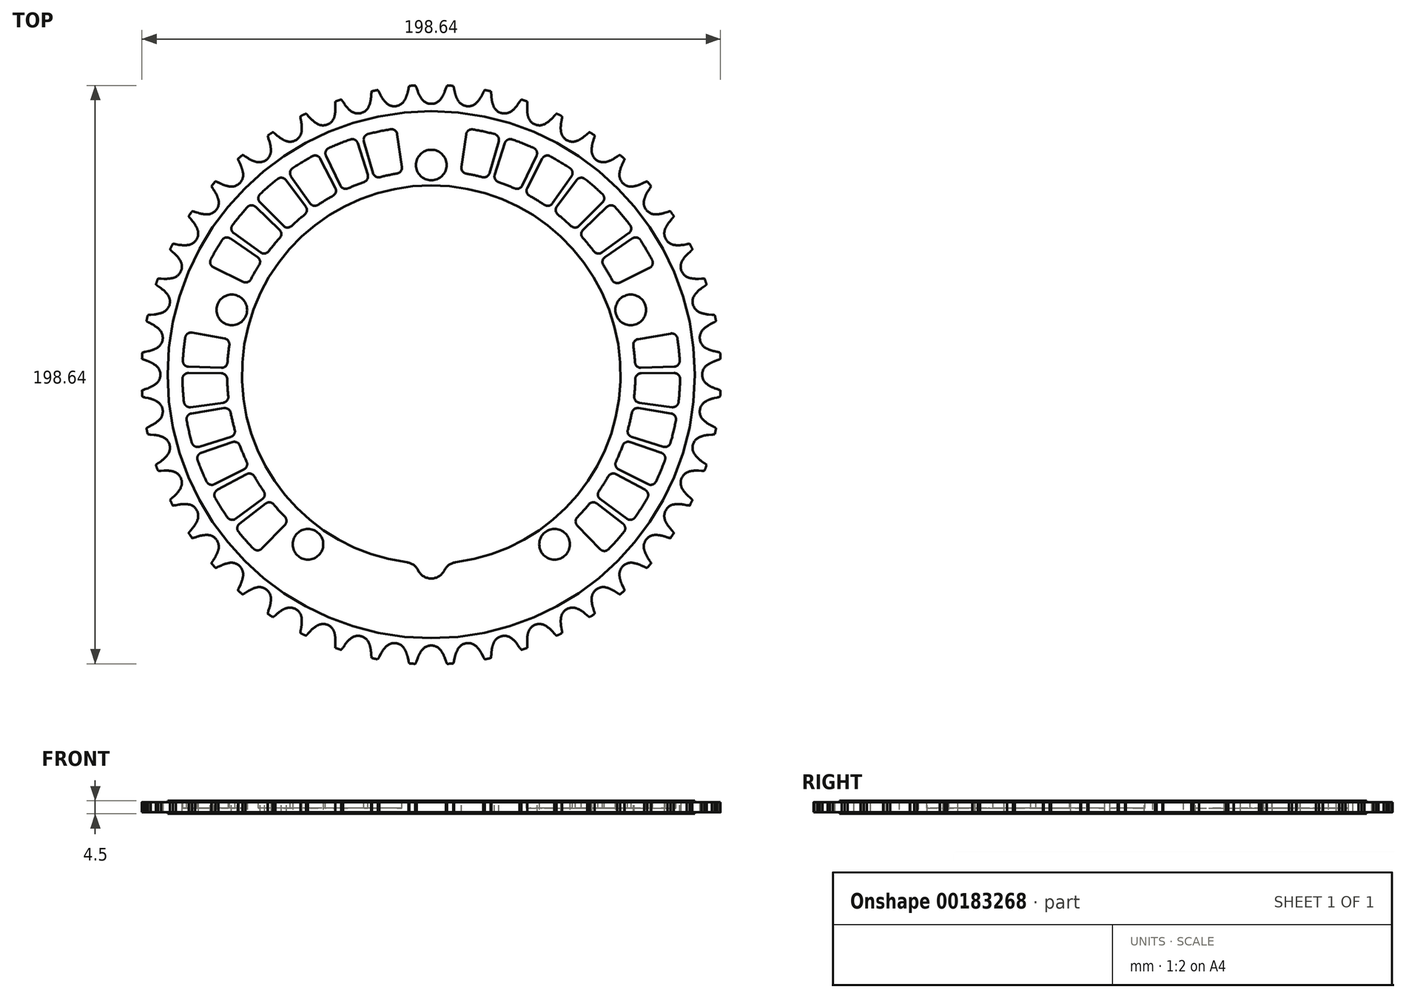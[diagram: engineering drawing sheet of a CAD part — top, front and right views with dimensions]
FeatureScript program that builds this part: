
annotation { "Feature Type Name" : "Feature", "Feature Type Description" : "" }
export const myFeature = defineFeature(function(context is Context, id is Id, definition is map)
    precondition{}
    {
        {
            var Q0;
            Q0=qCreatedBy(makeId("Top.planeOp"),FACE);
            var sketch = newSketch(context, id + "F0", { "sketchPlane" : qUnion([Q0])});
            skCircle(sketch, "E0", {"center": v(0, 0) * mm, "radius": 97.02 * mm, "construction": true});
            skArc(sketch, "E1", {"start": v(-4.67, 97.33) * mm, "mid": v(-4.05, 95.93) * mm, "end": v(-3.24, 94.65) * mm});
            skLineSegment(sketch, "E2", {"start": v(-4.67, 97.33) * mm, "end": v(-5.03, 98.35) * mm});
            skArc(sketch, "E3.trimOffspring", {"start": v(-3.24, 94.65) * mm, "mid": v(-1.81, 93.44) * mm, "end": v(0, 93) * mm});
            skArc(sketch, "E4.trimOffspring", {"start": v(-5.03, 98.35) * mm, "mid": v(-5.68, 99.7) * mm, "end": v(-6.61, 100.86) * mm});
            skArc(sketch, "E5.MirrorCS", {"start": v(3.24, 94.65) * mm, "mid": v(1.81, 93.44) * mm, "end": v(0, 93) * mm});
            skArc(sketch, "E6.MirrorCS", {"start": v(4.67, 97.33) * mm, "mid": v(4.05, 95.93) * mm, "end": v(3.24, 94.65) * mm});
            skLineSegment(sketch, "E7.MirrorCS", {"start": v(4.67, 97.33) * mm, "end": v(5.03, 98.35) * mm});
            skArc(sketch, "E8.MirrorCS", {"start": v(5.03, 98.35) * mm, "mid": v(5.68, 99.7) * mm, "end": v(6.61, 100.86) * mm});
            skCircle(sketch, "E9", {"center": v(0, 0) * mm, "radius": 99.47 * mm});
            skArc(sketch, "E10.1.0", {"start": v(-17.83, 96.85) * mm, "mid": v(-18.64, 98.1) * mm, "end": v(-19.72, 99.14) * mm});
            skLineSegment(sketch, "E10.1.1", {"start": v(-17.34, 95.88) * mm, "end": v(-17.83, 96.85) * mm});
            skArc(sketch, "E10.1.2", {"start": v(-17.34, 95.88) * mm, "mid": v(-16.54, 94.58) * mm, "end": v(-15.56, 93.41) * mm});
            skArc(sketch, "E10.1.3", {"start": v(-15.56, 93.41) * mm, "mid": v(-14, 92.4) * mm, "end": v(-12.14, 92.2) * mm});
            skArc(sketch, "E10.1.4", {"start": v(-9.14, 94.26) * mm, "mid": v(-10.4, 92.88) * mm, "end": v(-12.14, 92.2) * mm});
            skArc(sketch, "E10.1.5", {"start": v(-8.07, 97.1) * mm, "mid": v(-8.5, 95.64) * mm, "end": v(-9.14, 94.26) * mm});
            skLineSegment(sketch, "E10.1.6", {"start": v(-8.07, 97.1) * mm, "end": v(-7.85, 98.17) * mm});
            skArc(sketch, "E10.1.7", {"start": v(-7.85, 98.17) * mm, "mid": v(-7.39, 99.59) * mm, "end": v(-6.61, 100.86) * mm});
            skArc(sketch, "E10.2.0", {"start": v(-30.32, 93.7) * mm, "mid": v(-31.29, 94.83) * mm, "end": v(-32.5, 95.72) * mm});
            skLineSegment(sketch, "E10.2.1", {"start": v(-29.7, 92.8) * mm, "end": v(-30.32, 93.7) * mm});
            skArc(sketch, "E10.2.2", {"start": v(-29.7, 92.8) * mm, "mid": v(-28.74, 91.61) * mm, "end": v(-27.62, 90.58) * mm});
            skArc(sketch, "E10.2.3", {"start": v(-27.62, 90.58) * mm, "mid": v(-25.94, 89.79) * mm, "end": v(-24.07, 89.84) * mm});
            skArc(sketch, "E10.2.4", {"start": v(-21.37, 92.26) * mm, "mid": v(-22.43, 90.72) * mm, "end": v(-24.07, 89.84) * mm});
            skArc(sketch, "E10.2.5", {"start": v(-20.68, 95.22) * mm, "mid": v(-20.91, 93.71) * mm, "end": v(-21.37, 92.26) * mm});
            skLineSegment(sketch, "E10.2.6", {"start": v(-20.68, 95.22) * mm, "end": v(-20.6, 96.3) * mm});
            skArc(sketch, "E10.2.7", {"start": v(-20.6, 96.3) * mm, "mid": v(-20.32, 97.77) * mm, "end": v(-19.72, 99.14) * mm});
            skArc(sketch, "E10.3.0", {"start": v(-42.29, 88.94) * mm, "mid": v(-43.4, 89.94) * mm, "end": v(-44.7, 90.66) * mm});
            skLineSegment(sketch, "E10.3.1", {"start": v(-41.56, 88.13) * mm, "end": v(-42.29, 88.94) * mm});
            skArc(sketch, "E10.3.2", {"start": v(-41.56, 88.13) * mm, "mid": v(-40.46, 87.08) * mm, "end": v(-39.21, 86.2) * mm});
            skArc(sketch, "E10.3.3", {"start": v(-39.21, 86.2) * mm, "mid": v(-37.43, 85.63) * mm, "end": v(-35.6, 85.93) * mm});
            skArc(sketch, "E10.3.4", {"start": v(-33.23, 88.68) * mm, "mid": v(-34.08, 87.02) * mm, "end": v(-35.6, 85.93) * mm});
            skArc(sketch, "E10.3.5", {"start": v(-32.93, 91.7) * mm, "mid": v(-32.97, 90.18) * mm, "end": v(-33.23, 88.68) * mm});
            skLineSegment(sketch, "E10.3.6", {"start": v(-32.93, 91.7) * mm, "end": v(-32.99, 92.79) * mm});
            skArc(sketch, "E10.3.7", {"start": v(-32.99, 92.79) * mm, "mid": v(-32.91, 94.28) * mm, "end": v(-32.5, 95.72) * mm});
            skArc(sketch, "E10.4.0", {"start": v(-53.53, 82.66) * mm, "mid": v(-54.76, 83.5) * mm, "end": v(-56.16, 84.05) * mm});
            skLineSegment(sketch, "E10.4.1", {"start": v(-52.7, 81.95) * mm, "end": v(-53.53, 82.66) * mm});
            skArc(sketch, "E10.4.2", {"start": v(-52.7, 81.95) * mm, "mid": v(-51.48, 81.05) * mm, "end": v(-50.13, 80.35) * mm});
            skArc(sketch, "E10.4.3", {"start": v(-50.13, 80.35) * mm, "mid": v(-48.3, 80.01) * mm, "end": v(-46.5, 80.55) * mm});
            skArc(sketch, "E10.4.4", {"start": v(-44.52, 83.58) * mm, "mid": v(-45.15, 81.83) * mm, "end": v(-46.5, 80.55) * mm});
            skArc(sketch, "E10.4.5", {"start": v(-44.62, 86.62) * mm, "mid": v(-44.46, 85.1) * mm, "end": v(-44.52, 83.58) * mm});
            skLineSegment(sketch, "E10.4.6", {"start": v(-44.62, 86.62) * mm, "end": v(-44.82, 87.7) * mm});
            skArc(sketch, "E10.4.7", {"start": v(-44.82, 87.7) * mm, "mid": v(-44.93, 89.18) * mm, "end": v(-44.7, 90.66) * mm});
            skArc(sketch, "E10.5.0", {"start": v(-63.87, 74.96) * mm, "mid": v(-65.2, 75.64) * mm, "end": v(-66.65, 76) * mm});
            skLineSegment(sketch, "E10.5.1", {"start": v(-62.96, 74.37) * mm, "end": v(-63.87, 74.96) * mm});
            skArc(sketch, "E10.5.2", {"start": v(-62.96, 74.37) * mm, "mid": v(-61.62, 73.64) * mm, "end": v(-60.18, 73.12) * mm});
            skArc(sketch, "E10.5.3", {"start": v(-60.18, 73.12) * mm, "mid": v(-58.32, 73.03) * mm, "end": v(-56.62, 73.79) * mm});
            skArc(sketch, "E10.5.4", {"start": v(-55.05, 77.06) * mm, "mid": v(-55.44, 75.23) * mm, "end": v(-56.62, 73.79) * mm});
            skArc(sketch, "E10.5.5", {"start": v(-55.54, 80.06) * mm, "mid": v(-55.18, 78.58) * mm, "end": v(-55.05, 77.06) * mm});
            skLineSegment(sketch, "E10.5.6", {"start": v(-55.54, 80.06) * mm, "end": v(-55.88, 81.1) * mm});
            skArc(sketch, "E10.5.7", {"start": v(-55.88, 81.1) * mm, "mid": v(-56.2, 82.55) * mm, "end": v(-56.16, 84.05) * mm});
            skArc(sketch, "E10.6.0", {"start": v(-73.1, 65.98) * mm, "mid": v(-74.51, 66.49) * mm, "end": v(-76, 66.65) * mm});
            skLineSegment(sketch, "E10.6.1", {"start": v(-72.12, 65.51) * mm, "end": v(-73.1, 65.98) * mm});
            skArc(sketch, "E10.6.2", {"start": v(-72.12, 65.51) * mm, "mid": v(-70.7, 64.97) * mm, "end": v(-69.21, 64.64) * mm});
            skArc(sketch, "E10.6.3", {"start": v(-69.21, 64.64) * mm, "mid": v(-67.35, 64.79) * mm, "end": v(-65.76, 65.76) * mm});
            skArc(sketch, "E10.6.4", {"start": v(-64.64, 69.21) * mm, "mid": v(-64.79, 67.35) * mm, "end": v(-65.76, 65.76) * mm});
            skArc(sketch, "E10.6.5", {"start": v(-65.51, 72.12) * mm, "mid": v(-64.97, 70.7) * mm, "end": v(-64.64, 69.21) * mm});
            skLineSegment(sketch, "E10.6.6", {"start": v(-65.51, 72.12) * mm, "end": v(-65.98, 73.1) * mm});
            skArc(sketch, "E10.6.7", {"start": v(-65.98, 73.1) * mm, "mid": v(-66.49, 74.51) * mm, "end": v(-66.65, 76) * mm});
            skArc(sketch, "E10.7.0", {"start": v(-81.1, 55.88) * mm, "mid": v(-82.55, 56.2) * mm, "end": v(-84.05, 56.16) * mm});
            skLineSegment(sketch, "E10.7.1", {"start": v(-80.06, 55.54) * mm, "end": v(-81.1, 55.88) * mm});
            skArc(sketch, "E10.7.2", {"start": v(-80.06, 55.54) * mm, "mid": v(-78.58, 55.18) * mm, "end": v(-77.06, 55.05) * mm});
            skArc(sketch, "E10.7.3", {"start": v(-77.06, 55.05) * mm, "mid": v(-75.23, 55.44) * mm, "end": v(-73.79, 56.62) * mm});
            skArc(sketch, "E10.7.4", {"start": v(-73.12, 60.18) * mm, "mid": v(-73.03, 58.32) * mm, "end": v(-73.79, 56.62) * mm});
            skArc(sketch, "E10.7.5", {"start": v(-74.37, 62.96) * mm, "mid": v(-73.64, 61.62) * mm, "end": v(-73.12, 60.18) * mm});
            skLineSegment(sketch, "E10.7.6", {"start": v(-74.37, 62.96) * mm, "end": v(-74.96, 63.87) * mm});
            skArc(sketch, "E10.7.7", {"start": v(-74.96, 63.87) * mm, "mid": v(-75.64, 65.2) * mm, "end": v(-76, 66.65) * mm});
            skArc(sketch, "E10.8.0", {"start": v(-87.7, 44.82) * mm, "mid": v(-89.18, 44.93) * mm, "end": v(-90.66, 44.7) * mm});
            skLineSegment(sketch, "E10.8.1", {"start": v(-86.62, 44.62) * mm, "end": v(-87.7, 44.82) * mm});
            skArc(sketch, "E10.8.2", {"start": v(-86.62, 44.62) * mm, "mid": v(-85.1, 44.46) * mm, "end": v(-83.58, 44.52) * mm});
            skArc(sketch, "E10.8.3", {"start": v(-83.58, 44.52) * mm, "mid": v(-81.83, 45.15) * mm, "end": v(-80.55, 46.5) * mm});
            skArc(sketch, "E10.8.4", {"start": v(-80.35, 50.13) * mm, "mid": v(-80.01, 48.3) * mm, "end": v(-80.55, 46.5) * mm});
            skArc(sketch, "E10.8.5", {"start": v(-81.95, 52.7) * mm, "mid": v(-81.05, 51.48) * mm, "end": v(-80.35, 50.13) * mm});
            skLineSegment(sketch, "E10.8.6", {"start": v(-81.95, 52.7) * mm, "end": v(-82.66, 53.53) * mm});
            skArc(sketch, "E10.8.7", {"start": v(-82.66, 53.53) * mm, "mid": v(-83.5, 54.76) * mm, "end": v(-84.05, 56.16) * mm});
            skArc(sketch, "E10.9.0", {"start": v(-92.79, 32.99) * mm, "mid": v(-94.28, 32.91) * mm, "end": v(-95.72, 32.5) * mm});
            skLineSegment(sketch, "E10.9.1", {"start": v(-91.7, 32.93) * mm, "end": v(-92.79, 32.99) * mm});
            skArc(sketch, "E10.9.2", {"start": v(-91.7, 32.93) * mm, "mid": v(-90.18, 32.97) * mm, "end": v(-88.68, 33.23) * mm});
            skArc(sketch, "E10.9.3", {"start": v(-88.68, 33.23) * mm, "mid": v(-87.02, 34.08) * mm, "end": v(-85.93, 35.6) * mm});
            skArc(sketch, "E10.9.4", {"start": v(-86.2, 39.21) * mm, "mid": v(-85.63, 37.43) * mm, "end": v(-85.93, 35.6) * mm});
            skArc(sketch, "E10.9.5", {"start": v(-88.13, 41.56) * mm, "mid": v(-87.08, 40.46) * mm, "end": v(-86.2, 39.21) * mm});
            skLineSegment(sketch, "E10.9.6", {"start": v(-88.13, 41.56) * mm, "end": v(-88.94, 42.29) * mm});
            skArc(sketch, "E10.9.7", {"start": v(-88.94, 42.29) * mm, "mid": v(-89.94, 43.4) * mm, "end": v(-90.66, 44.7) * mm});
            skArc(sketch, "E10.10.0", {"start": v(-96.3, 20.6) * mm, "mid": v(-97.77, 20.32) * mm, "end": v(-99.14, 19.72) * mm});
            skLineSegment(sketch, "E10.10.1", {"start": v(-95.22, 20.68) * mm, "end": v(-96.3, 20.6) * mm});
            skArc(sketch, "E10.10.2", {"start": v(-95.22, 20.68) * mm, "mid": v(-93.71, 20.91) * mm, "end": v(-92.26, 21.37) * mm});
            skArc(sketch, "E10.10.3", {"start": v(-92.26, 21.37) * mm, "mid": v(-90.72, 22.43) * mm, "end": v(-89.84, 24.07) * mm});
            skArc(sketch, "E10.10.4", {"start": v(-90.58, 27.62) * mm, "mid": v(-89.79, 25.94) * mm, "end": v(-89.84, 24.07) * mm});
            skArc(sketch, "E10.10.5", {"start": v(-92.8, 29.7) * mm, "mid": v(-91.61, 28.74) * mm, "end": v(-90.58, 27.62) * mm});
            skLineSegment(sketch, "E10.10.6", {"start": v(-92.8, 29.7) * mm, "end": v(-93.7, 30.32) * mm});
            skArc(sketch, "E10.10.7", {"start": v(-93.7, 30.32) * mm, "mid": v(-94.83, 31.29) * mm, "end": v(-95.72, 32.5) * mm});
            skArc(sketch, "E10.11.0", {"start": v(-98.17, 7.85) * mm, "mid": v(-99.59, 7.39) * mm, "end": v(-100.86, 6.61) * mm});
            skLineSegment(sketch, "E10.11.1", {"start": v(-97.1, 8.07) * mm, "end": v(-98.17, 7.85) * mm});
            skArc(sketch, "E10.11.2", {"start": v(-97.1, 8.07) * mm, "mid": v(-95.64, 8.5) * mm, "end": v(-94.26, 9.14) * mm});
            skArc(sketch, "E10.11.3", {"start": v(-94.26, 9.14) * mm, "mid": v(-92.88, 10.4) * mm, "end": v(-92.2, 12.14) * mm});
            skArc(sketch, "E10.11.4", {"start": v(-93.41, 15.56) * mm, "mid": v(-92.4, 14) * mm, "end": v(-92.2, 12.14) * mm});
            skArc(sketch, "E10.11.5", {"start": v(-95.88, 17.34) * mm, "mid": v(-94.58, 16.54) * mm, "end": v(-93.41, 15.56) * mm});
            skLineSegment(sketch, "E10.11.6", {"start": v(-95.88, 17.34) * mm, "end": v(-96.85, 17.83) * mm});
            skArc(sketch, "E10.11.7", {"start": v(-96.85, 17.83) * mm, "mid": v(-98.1, 18.64) * mm, "end": v(-99.14, 19.72) * mm});
            skArc(sketch, "E10.12.0", {"start": v(-98.35, -5.03) * mm, "mid": v(-99.7, -5.68) * mm, "end": v(-100.86, -6.61) * mm});
            skLineSegment(sketch, "E10.12.1", {"start": v(-97.33, -4.67) * mm, "end": v(-98.35, -5.03) * mm});
            skArc(sketch, "E10.12.2", {"start": v(-97.33, -4.67) * mm, "mid": v(-95.93, -4.05) * mm, "end": v(-94.65, -3.24) * mm});
            skArc(sketch, "E10.12.3", {"start": v(-94.65, -3.24) * mm, "mid": v(-93.44, -1.81) * mm, "end": v(-93, 0) * mm});
            skArc(sketch, "E10.12.4", {"start": v(-94.65, 3.24) * mm, "mid": v(-93.44, 1.81) * mm, "end": v(-93, 0) * mm});
            skArc(sketch, "E10.12.5", {"start": v(-97.33, 4.67) * mm, "mid": v(-95.93, 4.05) * mm, "end": v(-94.65, 3.24) * mm});
            skLineSegment(sketch, "E10.12.6", {"start": v(-97.33, 4.67) * mm, "end": v(-98.35, 5.03) * mm});
            skArc(sketch, "E10.12.7", {"start": v(-98.35, 5.03) * mm, "mid": v(-99.7, 5.68) * mm, "end": v(-100.86, 6.61) * mm});
            skArc(sketch, "E10.13.0", {"start": v(-96.85, -17.83) * mm, "mid": v(-98.1, -18.64) * mm, "end": v(-99.14, -19.72) * mm});
            skLineSegment(sketch, "E10.13.1", {"start": v(-95.88, -17.34) * mm, "end": v(-96.85, -17.83) * mm});
            skArc(sketch, "E10.13.2", {"start": v(-95.88, -17.34) * mm, "mid": v(-94.58, -16.54) * mm, "end": v(-93.41, -15.56) * mm});
            skArc(sketch, "E10.13.3", {"start": v(-93.41, -15.56) * mm, "mid": v(-92.4, -14) * mm, "end": v(-92.2, -12.14) * mm});
            skArc(sketch, "E10.13.4", {"start": v(-94.26, -9.14) * mm, "mid": v(-92.88, -10.4) * mm, "end": v(-92.2, -12.14) * mm});
            skArc(sketch, "E10.13.5", {"start": v(-97.1, -8.07) * mm, "mid": v(-95.64, -8.5) * mm, "end": v(-94.26, -9.14) * mm});
            skLineSegment(sketch, "E10.13.6", {"start": v(-97.1, -8.07) * mm, "end": v(-98.17, -7.85) * mm});
            skArc(sketch, "E10.13.7", {"start": v(-98.17, -7.85) * mm, "mid": v(-99.59, -7.39) * mm, "end": v(-100.86, -6.61) * mm});
            skArc(sketch, "E10.14.0", {"start": v(-93.7, -30.32) * mm, "mid": v(-94.83, -31.29) * mm, "end": v(-95.72, -32.5) * mm});
            skLineSegment(sketch, "E10.14.1", {"start": v(-92.8, -29.7) * mm, "end": v(-93.7, -30.32) * mm});
            skArc(sketch, "E10.14.2", {"start": v(-92.8, -29.7) * mm, "mid": v(-91.61, -28.74) * mm, "end": v(-90.58, -27.62) * mm});
            skArc(sketch, "E10.14.3", {"start": v(-90.58, -27.62) * mm, "mid": v(-89.79, -25.94) * mm, "end": v(-89.84, -24.07) * mm});
            skArc(sketch, "E10.14.4", {"start": v(-92.26, -21.37) * mm, "mid": v(-90.72, -22.43) * mm, "end": v(-89.84, -24.07) * mm});
            skArc(sketch, "E10.14.5", {"start": v(-95.22, -20.68) * mm, "mid": v(-93.71, -20.91) * mm, "end": v(-92.26, -21.37) * mm});
            skLineSegment(sketch, "E10.14.6", {"start": v(-95.22, -20.68) * mm, "end": v(-96.3, -20.6) * mm});
            skArc(sketch, "E10.14.7", {"start": v(-96.3, -20.6) * mm, "mid": v(-97.77, -20.32) * mm, "end": v(-99.14, -19.72) * mm});
            skArc(sketch, "E10.15.0", {"start": v(-88.94, -42.29) * mm, "mid": v(-89.94, -43.4) * mm, "end": v(-90.66, -44.7) * mm});
            skLineSegment(sketch, "E10.15.1", {"start": v(-88.13, -41.56) * mm, "end": v(-88.94, -42.29) * mm});
            skArc(sketch, "E10.15.2", {"start": v(-88.13, -41.56) * mm, "mid": v(-87.08, -40.46) * mm, "end": v(-86.2, -39.21) * mm});
            skArc(sketch, "E10.15.3", {"start": v(-86.2, -39.21) * mm, "mid": v(-85.63, -37.43) * mm, "end": v(-85.93, -35.6) * mm});
            skArc(sketch, "E10.15.4", {"start": v(-88.68, -33.23) * mm, "mid": v(-87.02, -34.08) * mm, "end": v(-85.93, -35.6) * mm});
            skArc(sketch, "E10.15.5", {"start": v(-91.7, -32.93) * mm, "mid": v(-90.18, -32.97) * mm, "end": v(-88.68, -33.23) * mm});
            skLineSegment(sketch, "E10.15.6", {"start": v(-91.7, -32.93) * mm, "end": v(-92.79, -32.99) * mm});
            skArc(sketch, "E10.15.7", {"start": v(-92.79, -32.99) * mm, "mid": v(-94.28, -32.91) * mm, "end": v(-95.72, -32.5) * mm});
            skArc(sketch, "E10.16.0", {"start": v(-82.66, -53.53) * mm, "mid": v(-83.5, -54.76) * mm, "end": v(-84.05, -56.16) * mm});
            skLineSegment(sketch, "E10.16.1", {"start": v(-81.95, -52.7) * mm, "end": v(-82.66, -53.53) * mm});
            skArc(sketch, "E10.16.2", {"start": v(-81.95, -52.7) * mm, "mid": v(-81.05, -51.48) * mm, "end": v(-80.35, -50.13) * mm});
            skArc(sketch, "E10.16.3", {"start": v(-80.35, -50.13) * mm, "mid": v(-80.01, -48.3) * mm, "end": v(-80.55, -46.5) * mm});
            skArc(sketch, "E10.16.4", {"start": v(-83.58, -44.52) * mm, "mid": v(-81.83, -45.15) * mm, "end": v(-80.55, -46.5) * mm});
            skArc(sketch, "E10.16.5", {"start": v(-86.62, -44.62) * mm, "mid": v(-85.1, -44.46) * mm, "end": v(-83.58, -44.52) * mm});
            skLineSegment(sketch, "E10.16.6", {"start": v(-86.62, -44.62) * mm, "end": v(-87.7, -44.82) * mm});
            skArc(sketch, "E10.16.7", {"start": v(-87.7, -44.82) * mm, "mid": v(-89.18, -44.93) * mm, "end": v(-90.66, -44.7) * mm});
            skArc(sketch, "E10.17.0", {"start": v(-74.96, -63.87) * mm, "mid": v(-75.64, -65.2) * mm, "end": v(-76, -66.65) * mm});
            skLineSegment(sketch, "E10.17.1", {"start": v(-74.37, -62.96) * mm, "end": v(-74.96, -63.87) * mm});
            skArc(sketch, "E10.17.2", {"start": v(-74.37, -62.96) * mm, "mid": v(-73.64, -61.62) * mm, "end": v(-73.12, -60.18) * mm});
            skArc(sketch, "E10.17.3", {"start": v(-73.12, -60.18) * mm, "mid": v(-73.03, -58.32) * mm, "end": v(-73.79, -56.62) * mm});
            skArc(sketch, "E10.17.4", {"start": v(-77.06, -55.05) * mm, "mid": v(-75.23, -55.44) * mm, "end": v(-73.79, -56.62) * mm});
            skArc(sketch, "E10.17.5", {"start": v(-80.06, -55.54) * mm, "mid": v(-78.58, -55.18) * mm, "end": v(-77.06, -55.05) * mm});
            skLineSegment(sketch, "E10.17.6", {"start": v(-80.06, -55.54) * mm, "end": v(-81.1, -55.88) * mm});
            skArc(sketch, "E10.17.7", {"start": v(-81.1, -55.88) * mm, "mid": v(-82.55, -56.2) * mm, "end": v(-84.05, -56.16) * mm});
            skArc(sketch, "E10.18.0", {"start": v(-65.98, -73.1) * mm, "mid": v(-66.49, -74.51) * mm, "end": v(-66.65, -76) * mm});
            skLineSegment(sketch, "E10.18.1", {"start": v(-65.51, -72.12) * mm, "end": v(-65.98, -73.1) * mm});
            skArc(sketch, "E10.18.2", {"start": v(-65.51, -72.12) * mm, "mid": v(-64.97, -70.7) * mm, "end": v(-64.64, -69.21) * mm});
            skArc(sketch, "E10.18.3", {"start": v(-64.64, -69.21) * mm, "mid": v(-64.79, -67.35) * mm, "end": v(-65.76, -65.76) * mm});
            skArc(sketch, "E10.18.4", {"start": v(-69.21, -64.64) * mm, "mid": v(-67.35, -64.79) * mm, "end": v(-65.76, -65.76) * mm});
            skArc(sketch, "E10.18.5", {"start": v(-72.12, -65.51) * mm, "mid": v(-70.7, -64.97) * mm, "end": v(-69.21, -64.64) * mm});
            skLineSegment(sketch, "E10.18.6", {"start": v(-72.12, -65.51) * mm, "end": v(-73.1, -65.98) * mm});
            skArc(sketch, "E10.18.7", {"start": v(-73.1, -65.98) * mm, "mid": v(-74.51, -66.49) * mm, "end": v(-76, -66.65) * mm});
            skArc(sketch, "E10.19.0", {"start": v(-55.88, -81.1) * mm, "mid": v(-56.2, -82.55) * mm, "end": v(-56.16, -84.05) * mm});
            skLineSegment(sketch, "E10.19.1", {"start": v(-55.54, -80.06) * mm, "end": v(-55.88, -81.1) * mm});
            skArc(sketch, "E10.19.2", {"start": v(-55.54, -80.06) * mm, "mid": v(-55.18, -78.58) * mm, "end": v(-55.05, -77.06) * mm});
            skArc(sketch, "E10.19.3", {"start": v(-55.05, -77.06) * mm, "mid": v(-55.44, -75.23) * mm, "end": v(-56.62, -73.79) * mm});
            skArc(sketch, "E10.19.4", {"start": v(-60.18, -73.12) * mm, "mid": v(-58.32, -73.03) * mm, "end": v(-56.62, -73.79) * mm});
            skArc(sketch, "E10.19.5", {"start": v(-62.96, -74.37) * mm, "mid": v(-61.62, -73.64) * mm, "end": v(-60.18, -73.12) * mm});
            skLineSegment(sketch, "E10.19.6", {"start": v(-62.96, -74.37) * mm, "end": v(-63.87, -74.96) * mm});
            skArc(sketch, "E10.19.7", {"start": v(-63.87, -74.96) * mm, "mid": v(-65.2, -75.64) * mm, "end": v(-66.65, -76) * mm});
            skArc(sketch, "E10.20.0", {"start": v(-44.82, -87.7) * mm, "mid": v(-44.93, -89.18) * mm, "end": v(-44.7, -90.66) * mm});
            skLineSegment(sketch, "E10.20.1", {"start": v(-44.62, -86.62) * mm, "end": v(-44.82, -87.7) * mm});
            skArc(sketch, "E10.20.2", {"start": v(-44.62, -86.62) * mm, "mid": v(-44.46, -85.1) * mm, "end": v(-44.52, -83.58) * mm});
            skArc(sketch, "E10.20.3", {"start": v(-44.52, -83.58) * mm, "mid": v(-45.15, -81.83) * mm, "end": v(-46.5, -80.55) * mm});
            skArc(sketch, "E10.20.4", {"start": v(-50.13, -80.35) * mm, "mid": v(-48.3, -80.01) * mm, "end": v(-46.5, -80.55) * mm});
            skArc(sketch, "E10.20.5", {"start": v(-52.7, -81.95) * mm, "mid": v(-51.48, -81.05) * mm, "end": v(-50.13, -80.35) * mm});
            skLineSegment(sketch, "E10.20.6", {"start": v(-52.7, -81.95) * mm, "end": v(-53.53, -82.66) * mm});
            skArc(sketch, "E10.20.7", {"start": v(-53.53, -82.66) * mm, "mid": v(-54.76, -83.5) * mm, "end": v(-56.16, -84.05) * mm});
            skArc(sketch, "E10.21.0", {"start": v(-32.99, -92.79) * mm, "mid": v(-32.91, -94.28) * mm, "end": v(-32.5, -95.72) * mm});
            skLineSegment(sketch, "E10.21.1", {"start": v(-32.93, -91.7) * mm, "end": v(-32.99, -92.79) * mm});
            skArc(sketch, "E10.21.2", {"start": v(-32.93, -91.7) * mm, "mid": v(-32.97, -90.18) * mm, "end": v(-33.23, -88.68) * mm});
            skArc(sketch, "E10.21.3", {"start": v(-33.23, -88.68) * mm, "mid": v(-34.08, -87.02) * mm, "end": v(-35.6, -85.93) * mm});
            skArc(sketch, "E10.21.4", {"start": v(-39.21, -86.2) * mm, "mid": v(-37.43, -85.63) * mm, "end": v(-35.6, -85.93) * mm});
            skArc(sketch, "E10.21.5", {"start": v(-41.56, -88.13) * mm, "mid": v(-40.46, -87.08) * mm, "end": v(-39.21, -86.2) * mm});
            skLineSegment(sketch, "E10.21.6", {"start": v(-41.56, -88.13) * mm, "end": v(-42.29, -88.94) * mm});
            skArc(sketch, "E10.21.7", {"start": v(-42.29, -88.94) * mm, "mid": v(-43.4, -89.94) * mm, "end": v(-44.7, -90.66) * mm});
            skArc(sketch, "E10.22.0", {"start": v(-20.6, -96.3) * mm, "mid": v(-20.32, -97.77) * mm, "end": v(-19.72, -99.14) * mm});
            skLineSegment(sketch, "E10.22.1", {"start": v(-20.68, -95.22) * mm, "end": v(-20.6, -96.3) * mm});
            skArc(sketch, "E10.22.2", {"start": v(-20.68, -95.22) * mm, "mid": v(-20.91, -93.71) * mm, "end": v(-21.37, -92.26) * mm});
            skArc(sketch, "E10.22.3", {"start": v(-21.37, -92.26) * mm, "mid": v(-22.43, -90.72) * mm, "end": v(-24.07, -89.84) * mm});
            skArc(sketch, "E10.22.4", {"start": v(-27.62, -90.58) * mm, "mid": v(-25.94, -89.79) * mm, "end": v(-24.07, -89.84) * mm});
            skArc(sketch, "E10.22.5", {"start": v(-29.7, -92.8) * mm, "mid": v(-28.74, -91.61) * mm, "end": v(-27.62, -90.58) * mm});
            skLineSegment(sketch, "E10.22.6", {"start": v(-29.7, -92.8) * mm, "end": v(-30.32, -93.7) * mm});
            skArc(sketch, "E10.22.7", {"start": v(-30.32, -93.7) * mm, "mid": v(-31.29, -94.83) * mm, "end": v(-32.5, -95.72) * mm});
            skArc(sketch, "E10.23.0", {"start": v(-7.85, -98.17) * mm, "mid": v(-7.39, -99.59) * mm, "end": v(-6.61, -100.86) * mm});
            skLineSegment(sketch, "E10.23.1", {"start": v(-8.07, -97.1) * mm, "end": v(-7.85, -98.17) * mm});
            skArc(sketch, "E10.23.2", {"start": v(-8.07, -97.1) * mm, "mid": v(-8.5, -95.64) * mm, "end": v(-9.14, -94.26) * mm});
            skArc(sketch, "E10.23.3", {"start": v(-9.14, -94.26) * mm, "mid": v(-10.4, -92.88) * mm, "end": v(-12.14, -92.2) * mm});
            skArc(sketch, "E10.23.4", {"start": v(-15.56, -93.41) * mm, "mid": v(-14, -92.4) * mm, "end": v(-12.14, -92.2) * mm});
            skArc(sketch, "E10.23.5", {"start": v(-17.34, -95.88) * mm, "mid": v(-16.54, -94.58) * mm, "end": v(-15.56, -93.41) * mm});
            skLineSegment(sketch, "E10.23.6", {"start": v(-17.34, -95.88) * mm, "end": v(-17.83, -96.85) * mm});
            skArc(sketch, "E10.23.7", {"start": v(-17.83, -96.85) * mm, "mid": v(-18.64, -98.1) * mm, "end": v(-19.72, -99.14) * mm});
            skArc(sketch, "E10.24.0", {"start": v(5.03, -98.35) * mm, "mid": v(5.68, -99.7) * mm, "end": v(6.61, -100.86) * mm});
            skLineSegment(sketch, "E10.24.1", {"start": v(4.67, -97.33) * mm, "end": v(5.03, -98.35) * mm});
            skArc(sketch, "E10.24.2", {"start": v(4.67, -97.33) * mm, "mid": v(4.05, -95.93) * mm, "end": v(3.24, -94.65) * mm});
            skArc(sketch, "E10.24.3", {"start": v(3.24, -94.65) * mm, "mid": v(1.81, -93.44) * mm, "end": v(0, -93) * mm});
            skArc(sketch, "E10.24.4", {"start": v(-3.24, -94.65) * mm, "mid": v(-1.81, -93.44) * mm, "end": v(0, -93) * mm});
            skArc(sketch, "E10.24.5", {"start": v(-4.67, -97.33) * mm, "mid": v(-4.05, -95.93) * mm, "end": v(-3.24, -94.65) * mm});
            skLineSegment(sketch, "E10.24.6", {"start": v(-4.67, -97.33) * mm, "end": v(-5.03, -98.35) * mm});
            skArc(sketch, "E10.24.7", {"start": v(-5.03, -98.35) * mm, "mid": v(-5.68, -99.7) * mm, "end": v(-6.61, -100.86) * mm});
            skArc(sketch, "E10.25.0", {"start": v(17.83, -96.85) * mm, "mid": v(18.64, -98.1) * mm, "end": v(19.72, -99.14) * mm});
            skLineSegment(sketch, "E10.25.1", {"start": v(17.34, -95.88) * mm, "end": v(17.83, -96.85) * mm});
            skArc(sketch, "E10.25.2", {"start": v(17.34, -95.88) * mm, "mid": v(16.54, -94.58) * mm, "end": v(15.56, -93.41) * mm});
            skArc(sketch, "E10.25.3", {"start": v(15.56, -93.41) * mm, "mid": v(14, -92.4) * mm, "end": v(12.14, -92.2) * mm});
            skArc(sketch, "E10.25.4", {"start": v(9.14, -94.26) * mm, "mid": v(10.4, -92.88) * mm, "end": v(12.14, -92.2) * mm});
            skArc(sketch, "E10.25.5", {"start": v(8.07, -97.1) * mm, "mid": v(8.5, -95.64) * mm, "end": v(9.14, -94.26) * mm});
            skLineSegment(sketch, "E10.25.6", {"start": v(8.07, -97.1) * mm, "end": v(7.85, -98.17) * mm});
            skArc(sketch, "E10.25.7", {"start": v(7.85, -98.17) * mm, "mid": v(7.39, -99.59) * mm, "end": v(6.61, -100.86) * mm});
            skArc(sketch, "E10.26.0", {"start": v(30.32, -93.7) * mm, "mid": v(31.29, -94.83) * mm, "end": v(32.5, -95.72) * mm});
            skLineSegment(sketch, "E10.26.1", {"start": v(29.7, -92.8) * mm, "end": v(30.32, -93.7) * mm});
            skArc(sketch, "E10.26.2", {"start": v(29.7, -92.8) * mm, "mid": v(28.74, -91.61) * mm, "end": v(27.62, -90.58) * mm});
            skArc(sketch, "E10.26.3", {"start": v(27.62, -90.58) * mm, "mid": v(25.94, -89.79) * mm, "end": v(24.07, -89.84) * mm});
            skArc(sketch, "E10.26.4", {"start": v(21.37, -92.26) * mm, "mid": v(22.43, -90.72) * mm, "end": v(24.07, -89.84) * mm});
            skArc(sketch, "E10.26.5", {"start": v(20.68, -95.22) * mm, "mid": v(20.91, -93.71) * mm, "end": v(21.37, -92.26) * mm});
            skLineSegment(sketch, "E10.26.6", {"start": v(20.68, -95.22) * mm, "end": v(20.6, -96.3) * mm});
            skArc(sketch, "E10.26.7", {"start": v(20.6, -96.3) * mm, "mid": v(20.32, -97.77) * mm, "end": v(19.72, -99.14) * mm});
            skArc(sketch, "E10.27.0", {"start": v(42.29, -88.94) * mm, "mid": v(43.4, -89.94) * mm, "end": v(44.7, -90.66) * mm});
            skLineSegment(sketch, "E10.27.1", {"start": v(41.56, -88.13) * mm, "end": v(42.29, -88.94) * mm});
            skArc(sketch, "E10.27.2", {"start": v(41.56, -88.13) * mm, "mid": v(40.46, -87.08) * mm, "end": v(39.21, -86.2) * mm});
            skArc(sketch, "E10.27.3", {"start": v(39.21, -86.2) * mm, "mid": v(37.43, -85.63) * mm, "end": v(35.6, -85.93) * mm});
            skArc(sketch, "E10.27.4", {"start": v(33.23, -88.68) * mm, "mid": v(34.08, -87.02) * mm, "end": v(35.6, -85.93) * mm});
            skArc(sketch, "E10.27.5", {"start": v(32.93, -91.7) * mm, "mid": v(32.97, -90.18) * mm, "end": v(33.23, -88.68) * mm});
            skLineSegment(sketch, "E10.27.6", {"start": v(32.93, -91.7) * mm, "end": v(32.99, -92.79) * mm});
            skArc(sketch, "E10.27.7", {"start": v(32.99, -92.79) * mm, "mid": v(32.91, -94.28) * mm, "end": v(32.5, -95.72) * mm});
            skArc(sketch, "E10.28.0", {"start": v(53.53, -82.66) * mm, "mid": v(54.76, -83.5) * mm, "end": v(56.16, -84.05) * mm});
            skLineSegment(sketch, "E10.28.1", {"start": v(52.7, -81.95) * mm, "end": v(53.53, -82.66) * mm});
            skArc(sketch, "E10.28.2", {"start": v(52.7, -81.95) * mm, "mid": v(51.48, -81.05) * mm, "end": v(50.13, -80.35) * mm});
            skArc(sketch, "E10.28.3", {"start": v(50.13, -80.35) * mm, "mid": v(48.3, -80.01) * mm, "end": v(46.5, -80.55) * mm});
            skArc(sketch, "E10.28.4", {"start": v(44.52, -83.58) * mm, "mid": v(45.15, -81.83) * mm, "end": v(46.5, -80.55) * mm});
            skArc(sketch, "E10.28.5", {"start": v(44.62, -86.62) * mm, "mid": v(44.46, -85.1) * mm, "end": v(44.52, -83.58) * mm});
            skLineSegment(sketch, "E10.28.6", {"start": v(44.62, -86.62) * mm, "end": v(44.82, -87.7) * mm});
            skArc(sketch, "E10.28.7", {"start": v(44.82, -87.7) * mm, "mid": v(44.93, -89.18) * mm, "end": v(44.7, -90.66) * mm});
            skArc(sketch, "E10.29.0", {"start": v(63.87, -74.96) * mm, "mid": v(65.2, -75.64) * mm, "end": v(66.65, -76) * mm});
            skLineSegment(sketch, "E10.29.1", {"start": v(62.96, -74.37) * mm, "end": v(63.87, -74.96) * mm});
            skArc(sketch, "E10.29.2", {"start": v(62.96, -74.37) * mm, "mid": v(61.62, -73.64) * mm, "end": v(60.18, -73.12) * mm});
            skArc(sketch, "E10.29.3", {"start": v(60.18, -73.12) * mm, "mid": v(58.32, -73.03) * mm, "end": v(56.62, -73.79) * mm});
            skArc(sketch, "E10.29.4", {"start": v(55.05, -77.06) * mm, "mid": v(55.44, -75.23) * mm, "end": v(56.62, -73.79) * mm});
            skArc(sketch, "E10.29.5", {"start": v(55.54, -80.06) * mm, "mid": v(55.18, -78.58) * mm, "end": v(55.05, -77.06) * mm});
            skLineSegment(sketch, "E10.29.6", {"start": v(55.54, -80.06) * mm, "end": v(55.88, -81.1) * mm});
            skArc(sketch, "E10.29.7", {"start": v(55.88, -81.1) * mm, "mid": v(56.2, -82.55) * mm, "end": v(56.16, -84.05) * mm});
            skArc(sketch, "E10.30.0", {"start": v(73.1, -65.98) * mm, "mid": v(74.51, -66.49) * mm, "end": v(76, -66.65) * mm});
            skLineSegment(sketch, "E10.30.1", {"start": v(72.12, -65.51) * mm, "end": v(73.1, -65.98) * mm});
            skArc(sketch, "E10.30.2", {"start": v(72.12, -65.51) * mm, "mid": v(70.7, -64.97) * mm, "end": v(69.21, -64.64) * mm});
            skArc(sketch, "E10.30.3", {"start": v(69.21, -64.64) * mm, "mid": v(67.35, -64.79) * mm, "end": v(65.76, -65.76) * mm});
            skArc(sketch, "E10.30.4", {"start": v(64.64, -69.21) * mm, "mid": v(64.79, -67.35) * mm, "end": v(65.76, -65.76) * mm});
            skArc(sketch, "E10.30.5", {"start": v(65.51, -72.12) * mm, "mid": v(64.97, -70.7) * mm, "end": v(64.64, -69.21) * mm});
            skLineSegment(sketch, "E10.30.6", {"start": v(65.51, -72.12) * mm, "end": v(65.98, -73.1) * mm});
            skArc(sketch, "E10.30.7", {"start": v(65.98, -73.1) * mm, "mid": v(66.49, -74.51) * mm, "end": v(66.65, -76) * mm});
            skArc(sketch, "E10.31.0", {"start": v(81.1, -55.88) * mm, "mid": v(82.55, -56.2) * mm, "end": v(84.05, -56.16) * mm});
            skLineSegment(sketch, "E10.31.1", {"start": v(80.06, -55.54) * mm, "end": v(81.1, -55.88) * mm});
            skArc(sketch, "E10.31.2", {"start": v(80.06, -55.54) * mm, "mid": v(78.58, -55.18) * mm, "end": v(77.06, -55.05) * mm});
            skArc(sketch, "E10.31.3", {"start": v(77.06, -55.05) * mm, "mid": v(75.23, -55.44) * mm, "end": v(73.79, -56.62) * mm});
            skArc(sketch, "E10.31.4", {"start": v(73.12, -60.18) * mm, "mid": v(73.03, -58.32) * mm, "end": v(73.79, -56.62) * mm});
            skArc(sketch, "E10.31.5", {"start": v(74.37, -62.96) * mm, "mid": v(73.64, -61.62) * mm, "end": v(73.12, -60.18) * mm});
            skLineSegment(sketch, "E10.31.6", {"start": v(74.37, -62.96) * mm, "end": v(74.96, -63.87) * mm});
            skArc(sketch, "E10.31.7", {"start": v(74.96, -63.87) * mm, "mid": v(75.64, -65.2) * mm, "end": v(76, -66.65) * mm});
            skArc(sketch, "E10.32.0", {"start": v(87.7, -44.82) * mm, "mid": v(89.18, -44.93) * mm, "end": v(90.66, -44.7) * mm});
            skLineSegment(sketch, "E10.32.1", {"start": v(86.62, -44.62) * mm, "end": v(87.7, -44.82) * mm});
            skArc(sketch, "E10.32.2", {"start": v(86.62, -44.62) * mm, "mid": v(85.1, -44.46) * mm, "end": v(83.58, -44.52) * mm});
            skArc(sketch, "E10.32.3", {"start": v(83.58, -44.52) * mm, "mid": v(81.83, -45.15) * mm, "end": v(80.55, -46.5) * mm});
            skArc(sketch, "E10.32.4", {"start": v(80.35, -50.13) * mm, "mid": v(80.01, -48.3) * mm, "end": v(80.55, -46.5) * mm});
            skArc(sketch, "E10.32.5", {"start": v(81.95, -52.7) * mm, "mid": v(81.05, -51.48) * mm, "end": v(80.35, -50.13) * mm});
            skLineSegment(sketch, "E10.32.6", {"start": v(81.95, -52.7) * mm, "end": v(82.66, -53.53) * mm});
            skArc(sketch, "E10.32.7", {"start": v(82.66, -53.53) * mm, "mid": v(83.5, -54.76) * mm, "end": v(84.05, -56.16) * mm});
            skArc(sketch, "E10.33.0", {"start": v(92.79, -32.99) * mm, "mid": v(94.28, -32.91) * mm, "end": v(95.72, -32.5) * mm});
            skLineSegment(sketch, "E10.33.1", {"start": v(91.7, -32.93) * mm, "end": v(92.79, -32.99) * mm});
            skArc(sketch, "E10.33.2", {"start": v(91.7, -32.93) * mm, "mid": v(90.18, -32.97) * mm, "end": v(88.68, -33.23) * mm});
            skArc(sketch, "E10.33.3", {"start": v(88.68, -33.23) * mm, "mid": v(87.02, -34.08) * mm, "end": v(85.93, -35.6) * mm});
            skArc(sketch, "E10.33.4", {"start": v(86.2, -39.21) * mm, "mid": v(85.63, -37.43) * mm, "end": v(85.93, -35.6) * mm});
            skArc(sketch, "E10.33.5", {"start": v(88.13, -41.56) * mm, "mid": v(87.08, -40.46) * mm, "end": v(86.2, -39.21) * mm});
            skLineSegment(sketch, "E10.33.6", {"start": v(88.13, -41.56) * mm, "end": v(88.94, -42.29) * mm});
            skArc(sketch, "E10.33.7", {"start": v(88.94, -42.29) * mm, "mid": v(89.94, -43.4) * mm, "end": v(90.66, -44.7) * mm});
            skArc(sketch, "E10.34.0", {"start": v(96.3, -20.6) * mm, "mid": v(97.77, -20.32) * mm, "end": v(99.14, -19.72) * mm});
            skLineSegment(sketch, "E10.34.1", {"start": v(95.22, -20.68) * mm, "end": v(96.3, -20.6) * mm});
            skArc(sketch, "E10.34.2", {"start": v(95.22, -20.68) * mm, "mid": v(93.71, -20.91) * mm, "end": v(92.26, -21.37) * mm});
            skArc(sketch, "E10.34.3", {"start": v(92.26, -21.37) * mm, "mid": v(90.72, -22.43) * mm, "end": v(89.84, -24.07) * mm});
            skArc(sketch, "E10.34.4", {"start": v(90.58, -27.62) * mm, "mid": v(89.79, -25.94) * mm, "end": v(89.84, -24.07) * mm});
            skArc(sketch, "E10.34.5", {"start": v(92.8, -29.7) * mm, "mid": v(91.61, -28.74) * mm, "end": v(90.58, -27.62) * mm});
            skLineSegment(sketch, "E10.34.6", {"start": v(92.8, -29.7) * mm, "end": v(93.7, -30.32) * mm});
            skArc(sketch, "E10.34.7", {"start": v(93.7, -30.32) * mm, "mid": v(94.83, -31.29) * mm, "end": v(95.72, -32.5) * mm});
            skArc(sketch, "E10.35.0", {"start": v(98.17, -7.85) * mm, "mid": v(99.59, -7.39) * mm, "end": v(100.86, -6.61) * mm});
            skLineSegment(sketch, "E10.35.1", {"start": v(97.1, -8.07) * mm, "end": v(98.17, -7.85) * mm});
            skArc(sketch, "E10.35.2", {"start": v(97.1, -8.07) * mm, "mid": v(95.64, -8.5) * mm, "end": v(94.26, -9.14) * mm});
            skArc(sketch, "E10.35.3", {"start": v(94.26, -9.14) * mm, "mid": v(92.88, -10.4) * mm, "end": v(92.2, -12.14) * mm});
            skArc(sketch, "E10.35.4", {"start": v(93.41, -15.56) * mm, "mid": v(92.4, -14) * mm, "end": v(92.2, -12.14) * mm});
            skArc(sketch, "E10.35.5", {"start": v(95.88, -17.34) * mm, "mid": v(94.58, -16.54) * mm, "end": v(93.41, -15.56) * mm});
            skLineSegment(sketch, "E10.35.6", {"start": v(95.88, -17.34) * mm, "end": v(96.85, -17.83) * mm});
            skArc(sketch, "E10.35.7", {"start": v(96.85, -17.83) * mm, "mid": v(98.1, -18.64) * mm, "end": v(99.14, -19.72) * mm});
            skArc(sketch, "E10.36.0", {"start": v(98.35, 5.03) * mm, "mid": v(99.7, 5.68) * mm, "end": v(100.86, 6.61) * mm});
            skLineSegment(sketch, "E10.36.1", {"start": v(97.33, 4.67) * mm, "end": v(98.35, 5.03) * mm});
            skArc(sketch, "E10.36.2", {"start": v(97.33, 4.67) * mm, "mid": v(95.93, 4.05) * mm, "end": v(94.65, 3.24) * mm});
            skArc(sketch, "E10.36.3", {"start": v(94.65, 3.24) * mm, "mid": v(93.44, 1.81) * mm, "end": v(93, 0) * mm});
            skArc(sketch, "E10.36.4", {"start": v(94.65, -3.24) * mm, "mid": v(93.44, -1.81) * mm, "end": v(93, 0) * mm});
            skArc(sketch, "E10.36.5", {"start": v(97.33, -4.67) * mm, "mid": v(95.93, -4.05) * mm, "end": v(94.65, -3.24) * mm});
            skLineSegment(sketch, "E10.36.6", {"start": v(97.33, -4.67) * mm, "end": v(98.35, -5.03) * mm});
            skArc(sketch, "E10.36.7", {"start": v(98.35, -5.03) * mm, "mid": v(99.7, -5.68) * mm, "end": v(100.86, -6.61) * mm});
            skArc(sketch, "E10.37.0", {"start": v(96.85, 17.83) * mm, "mid": v(98.1, 18.64) * mm, "end": v(99.14, 19.72) * mm});
            skLineSegment(sketch, "E10.37.1", {"start": v(95.88, 17.34) * mm, "end": v(96.85, 17.83) * mm});
            skArc(sketch, "E10.37.2", {"start": v(95.88, 17.34) * mm, "mid": v(94.58, 16.54) * mm, "end": v(93.41, 15.56) * mm});
            skArc(sketch, "E10.37.3", {"start": v(93.41, 15.56) * mm, "mid": v(92.4, 14) * mm, "end": v(92.2, 12.14) * mm});
            skArc(sketch, "E10.37.4", {"start": v(94.26, 9.14) * mm, "mid": v(92.88, 10.4) * mm, "end": v(92.2, 12.14) * mm});
            skArc(sketch, "E10.37.5", {"start": v(97.1, 8.07) * mm, "mid": v(95.64, 8.5) * mm, "end": v(94.26, 9.14) * mm});
            skLineSegment(sketch, "E10.37.6", {"start": v(97.1, 8.07) * mm, "end": v(98.17, 7.85) * mm});
            skArc(sketch, "E10.37.7", {"start": v(98.17, 7.85) * mm, "mid": v(99.59, 7.39) * mm, "end": v(100.86, 6.61) * mm});
            skArc(sketch, "E10.38.0", {"start": v(93.7, 30.32) * mm, "mid": v(94.83, 31.29) * mm, "end": v(95.72, 32.5) * mm});
            skLineSegment(sketch, "E10.38.1", {"start": v(92.8, 29.7) * mm, "end": v(93.7, 30.32) * mm});
            skArc(sketch, "E10.38.2", {"start": v(92.8, 29.7) * mm, "mid": v(91.61, 28.74) * mm, "end": v(90.58, 27.62) * mm});
            skArc(sketch, "E10.38.3", {"start": v(90.58, 27.62) * mm, "mid": v(89.79, 25.94) * mm, "end": v(89.84, 24.07) * mm});
            skArc(sketch, "E10.38.4", {"start": v(92.26, 21.37) * mm, "mid": v(90.72, 22.43) * mm, "end": v(89.84, 24.07) * mm});
            skArc(sketch, "E10.38.5", {"start": v(95.22, 20.68) * mm, "mid": v(93.71, 20.91) * mm, "end": v(92.26, 21.37) * mm});
            skLineSegment(sketch, "E10.38.6", {"start": v(95.22, 20.68) * mm, "end": v(96.3, 20.6) * mm});
            skArc(sketch, "E10.38.7", {"start": v(96.3, 20.6) * mm, "mid": v(97.77, 20.32) * mm, "end": v(99.14, 19.72) * mm});
            skArc(sketch, "E10.39.0", {"start": v(88.94, 42.29) * mm, "mid": v(89.94, 43.4) * mm, "end": v(90.66, 44.7) * mm});
            skLineSegment(sketch, "E10.39.1", {"start": v(88.13, 41.56) * mm, "end": v(88.94, 42.29) * mm});
            skArc(sketch, "E10.39.2", {"start": v(88.13, 41.56) * mm, "mid": v(87.08, 40.46) * mm, "end": v(86.2, 39.21) * mm});
            skArc(sketch, "E10.39.3", {"start": v(86.2, 39.21) * mm, "mid": v(85.63, 37.43) * mm, "end": v(85.93, 35.6) * mm});
            skArc(sketch, "E10.39.4", {"start": v(88.68, 33.23) * mm, "mid": v(87.02, 34.08) * mm, "end": v(85.93, 35.6) * mm});
            skArc(sketch, "E10.39.5", {"start": v(91.7, 32.93) * mm, "mid": v(90.18, 32.97) * mm, "end": v(88.68, 33.23) * mm});
            skLineSegment(sketch, "E10.39.6", {"start": v(91.7, 32.93) * mm, "end": v(92.79, 32.99) * mm});
            skArc(sketch, "E10.39.7", {"start": v(92.79, 32.99) * mm, "mid": v(94.28, 32.91) * mm, "end": v(95.72, 32.5) * mm});
            skArc(sketch, "E10.40.0", {"start": v(82.66, 53.53) * mm, "mid": v(83.5, 54.76) * mm, "end": v(84.05, 56.16) * mm});
            skLineSegment(sketch, "E10.40.1", {"start": v(81.95, 52.7) * mm, "end": v(82.66, 53.53) * mm});
            skArc(sketch, "E10.40.2", {"start": v(81.95, 52.7) * mm, "mid": v(81.05, 51.48) * mm, "end": v(80.35, 50.13) * mm});
            skArc(sketch, "E10.40.3", {"start": v(80.35, 50.13) * mm, "mid": v(80.01, 48.3) * mm, "end": v(80.55, 46.5) * mm});
            skArc(sketch, "E10.40.4", {"start": v(83.58, 44.52) * mm, "mid": v(81.83, 45.15) * mm, "end": v(80.55, 46.5) * mm});
            skArc(sketch, "E10.40.5", {"start": v(86.62, 44.62) * mm, "mid": v(85.1, 44.46) * mm, "end": v(83.58, 44.52) * mm});
            skLineSegment(sketch, "E10.40.6", {"start": v(86.62, 44.62) * mm, "end": v(87.7, 44.82) * mm});
            skArc(sketch, "E10.40.7", {"start": v(87.7, 44.82) * mm, "mid": v(89.18, 44.93) * mm, "end": v(90.66, 44.7) * mm});
            skArc(sketch, "E10.41.0", {"start": v(74.96, 63.87) * mm, "mid": v(75.64, 65.2) * mm, "end": v(76, 66.65) * mm});
            skLineSegment(sketch, "E10.41.1", {"start": v(74.37, 62.96) * mm, "end": v(74.96, 63.87) * mm});
            skArc(sketch, "E10.41.2", {"start": v(74.37, 62.96) * mm, "mid": v(73.64, 61.62) * mm, "end": v(73.12, 60.18) * mm});
            skArc(sketch, "E10.41.3", {"start": v(73.12, 60.18) * mm, "mid": v(73.03, 58.32) * mm, "end": v(73.79, 56.62) * mm});
            skArc(sketch, "E10.41.4", {"start": v(77.06, 55.05) * mm, "mid": v(75.23, 55.44) * mm, "end": v(73.79, 56.62) * mm});
            skArc(sketch, "E10.41.5", {"start": v(80.06, 55.54) * mm, "mid": v(78.58, 55.18) * mm, "end": v(77.06, 55.05) * mm});
            skLineSegment(sketch, "E10.41.6", {"start": v(80.06, 55.54) * mm, "end": v(81.1, 55.88) * mm});
            skArc(sketch, "E10.41.7", {"start": v(81.1, 55.88) * mm, "mid": v(82.55, 56.2) * mm, "end": v(84.05, 56.16) * mm});
            skArc(sketch, "E10.42.0", {"start": v(65.98, 73.1) * mm, "mid": v(66.49, 74.51) * mm, "end": v(66.65, 76) * mm});
            skLineSegment(sketch, "E10.42.1", {"start": v(65.51, 72.12) * mm, "end": v(65.98, 73.1) * mm});
            skArc(sketch, "E10.42.2", {"start": v(65.51, 72.12) * mm, "mid": v(64.97, 70.7) * mm, "end": v(64.64, 69.21) * mm});
            skArc(sketch, "E10.42.3", {"start": v(64.64, 69.21) * mm, "mid": v(64.79, 67.35) * mm, "end": v(65.76, 65.76) * mm});
            skArc(sketch, "E10.42.4", {"start": v(69.21, 64.64) * mm, "mid": v(67.35, 64.79) * mm, "end": v(65.76, 65.76) * mm});
            skArc(sketch, "E10.42.5", {"start": v(72.12, 65.51) * mm, "mid": v(70.7, 64.97) * mm, "end": v(69.21, 64.64) * mm});
            skLineSegment(sketch, "E10.42.6", {"start": v(72.12, 65.51) * mm, "end": v(73.1, 65.98) * mm});
            skArc(sketch, "E10.42.7", {"start": v(73.1, 65.98) * mm, "mid": v(74.51, 66.49) * mm, "end": v(76, 66.65) * mm});
            skArc(sketch, "E10.43.0", {"start": v(55.88, 81.1) * mm, "mid": v(56.2, 82.55) * mm, "end": v(56.16, 84.05) * mm});
            skLineSegment(sketch, "E10.43.1", {"start": v(55.54, 80.06) * mm, "end": v(55.88, 81.1) * mm});
            skArc(sketch, "E10.43.2", {"start": v(55.54, 80.06) * mm, "mid": v(55.18, 78.58) * mm, "end": v(55.05, 77.06) * mm});
            skArc(sketch, "E10.43.3", {"start": v(55.05, 77.06) * mm, "mid": v(55.44, 75.23) * mm, "end": v(56.62, 73.79) * mm});
            skArc(sketch, "E10.43.4", {"start": v(60.18, 73.12) * mm, "mid": v(58.32, 73.03) * mm, "end": v(56.62, 73.79) * mm});
            skArc(sketch, "E10.43.5", {"start": v(62.96, 74.37) * mm, "mid": v(61.62, 73.64) * mm, "end": v(60.18, 73.12) * mm});
            skLineSegment(sketch, "E10.43.6", {"start": v(62.96, 74.37) * mm, "end": v(63.87, 74.96) * mm});
            skArc(sketch, "E10.43.7", {"start": v(63.87, 74.96) * mm, "mid": v(65.2, 75.64) * mm, "end": v(66.65, 76) * mm});
            skArc(sketch, "E10.44.0", {"start": v(44.82, 87.7) * mm, "mid": v(44.93, 89.18) * mm, "end": v(44.7, 90.66) * mm});
            skLineSegment(sketch, "E10.44.1", {"start": v(44.62, 86.62) * mm, "end": v(44.82, 87.7) * mm});
            skArc(sketch, "E10.44.2", {"start": v(44.62, 86.62) * mm, "mid": v(44.46, 85.1) * mm, "end": v(44.52, 83.58) * mm});
            skArc(sketch, "E10.44.3", {"start": v(44.52, 83.58) * mm, "mid": v(45.15, 81.83) * mm, "end": v(46.5, 80.55) * mm});
            skArc(sketch, "E10.44.4", {"start": v(50.13, 80.35) * mm, "mid": v(48.3, 80.01) * mm, "end": v(46.5, 80.55) * mm});
            skArc(sketch, "E10.44.5", {"start": v(52.7, 81.95) * mm, "mid": v(51.48, 81.05) * mm, "end": v(50.13, 80.35) * mm});
            skLineSegment(sketch, "E10.44.6", {"start": v(52.7, 81.95) * mm, "end": v(53.53, 82.66) * mm});
            skArc(sketch, "E10.44.7", {"start": v(53.53, 82.66) * mm, "mid": v(54.76, 83.5) * mm, "end": v(56.16, 84.05) * mm});
            skArc(sketch, "E10.45.0", {"start": v(32.99, 92.79) * mm, "mid": v(32.91, 94.28) * mm, "end": v(32.5, 95.72) * mm});
            skLineSegment(sketch, "E10.45.1", {"start": v(32.93, 91.7) * mm, "end": v(32.99, 92.79) * mm});
            skArc(sketch, "E10.45.2", {"start": v(32.93, 91.7) * mm, "mid": v(32.97, 90.18) * mm, "end": v(33.23, 88.68) * mm});
            skArc(sketch, "E10.45.3", {"start": v(33.23, 88.68) * mm, "mid": v(34.08, 87.02) * mm, "end": v(35.6, 85.93) * mm});
            skArc(sketch, "E10.45.4", {"start": v(39.21, 86.2) * mm, "mid": v(37.43, 85.63) * mm, "end": v(35.6, 85.93) * mm});
            skArc(sketch, "E10.45.5", {"start": v(41.56, 88.13) * mm, "mid": v(40.46, 87.08) * mm, "end": v(39.21, 86.2) * mm});
            skLineSegment(sketch, "E10.45.6", {"start": v(41.56, 88.13) * mm, "end": v(42.29, 88.94) * mm});
            skArc(sketch, "E10.45.7", {"start": v(42.29, 88.94) * mm, "mid": v(43.4, 89.94) * mm, "end": v(44.7, 90.66) * mm});
            skArc(sketch, "E10.46.0", {"start": v(20.6, 96.3) * mm, "mid": v(20.32, 97.77) * mm, "end": v(19.72, 99.14) * mm});
            skLineSegment(sketch, "E10.46.1", {"start": v(20.68, 95.22) * mm, "end": v(20.6, 96.3) * mm});
            skArc(sketch, "E10.46.2", {"start": v(20.68, 95.22) * mm, "mid": v(20.91, 93.71) * mm, "end": v(21.37, 92.26) * mm});
            skArc(sketch, "E10.46.3", {"start": v(21.37, 92.26) * mm, "mid": v(22.43, 90.72) * mm, "end": v(24.07, 89.84) * mm});
            skArc(sketch, "E10.46.4", {"start": v(27.62, 90.58) * mm, "mid": v(25.94, 89.79) * mm, "end": v(24.07, 89.84) * mm});
            skArc(sketch, "E10.46.5", {"start": v(29.7, 92.8) * mm, "mid": v(28.74, 91.61) * mm, "end": v(27.62, 90.58) * mm});
            skLineSegment(sketch, "E10.46.6", {"start": v(29.7, 92.8) * mm, "end": v(30.32, 93.7) * mm});
            skArc(sketch, "E10.46.7", {"start": v(30.32, 93.7) * mm, "mid": v(31.29, 94.83) * mm, "end": v(32.5, 95.72) * mm});
            skArc(sketch, "E10.47.0", {"start": v(7.85, 98.17) * mm, "mid": v(7.39, 99.59) * mm, "end": v(6.61, 100.86) * mm});
            skLineSegment(sketch, "E10.47.1", {"start": v(8.07, 97.1) * mm, "end": v(7.85, 98.17) * mm});
            skArc(sketch, "E10.47.2", {"start": v(8.07, 97.1) * mm, "mid": v(8.5, 95.64) * mm, "end": v(9.14, 94.26) * mm});
            skArc(sketch, "E10.47.3", {"start": v(9.14, 94.26) * mm, "mid": v(10.4, 92.88) * mm, "end": v(12.14, 92.2) * mm});
            skArc(sketch, "E10.47.4", {"start": v(15.56, 93.41) * mm, "mid": v(14, 92.4) * mm, "end": v(12.14, 92.2) * mm});
            skArc(sketch, "E10.47.5", {"start": v(17.34, 95.88) * mm, "mid": v(16.54, 94.58) * mm, "end": v(15.56, 93.41) * mm});
            skLineSegment(sketch, "E10.47.6", {"start": v(17.34, 95.88) * mm, "end": v(17.83, 96.85) * mm});
            skArc(sketch, "E10.47.7", {"start": v(17.83, 96.85) * mm, "mid": v(18.64, 98.1) * mm, "end": v(19.72, 99.14) * mm});
            skCircle(sketch, "E11", {"center": v(0, 72) * mm, "radius": 5.25 * mm});
            skCircle(sketch, "E12.1.0", {"center": v(-68.48, 22.25) * mm, "radius": 5.25 * mm});
            skCircle(sketch, "E12.2.0", {"center": v(-42.32, -58.25) * mm, "radius": 5.25 * mm});
            skCircle(sketch, "E12.3.0", {"center": v(42.32, -58.25) * mm, "radius": 5.25 * mm});
            skCircle(sketch, "E12.4.0", {"center": v(68.48, 22.25) * mm, "radius": 5.25 * mm});
            skCircle(sketch, "E13", {"center": v(0, 0) * mm, "radius": 65 * mm});
            skCircle(sketch, "E14", {"center": v(0, -65) * mm, "radius": 5 * mm});
            skCircle(sketch, "E15", {"center": v(0, 0) * mm, "radius": 90.5 * mm});
            skSolve(sketch);
        }
        {
            var Q0;
            Q0=makeQuery(id+"F0.imprint","IMPRINT",FACE,{"disambiguationData":[TD([[makeQuery(id+"F0.imprint","IMPRINT",EDGE,{"derivedFrom":sQuery(id+"F0.wireOp",EDGE,"E11")}),-1.0]])]});
            extrude(context, id + "F1", {"entities" : qUnion([Q0]), "endBound" : BoundingType.SYMMETRIC, "depth" : 4.5 * mm});
        }
        {
            var Q0;
            Q0=makeQuery(id+"F0.imprint","IMPRINT",FACE,{"disambiguationData":[TD([[makeQuery(id+"F0.imprint","IMPRINT",EDGE,{"derivedFrom":sQuery(id+"F0.wireOp",EDGE,"E1")}),-1.0]])]});
            extrude(context, id + "F2", {"entities" : qUnion([Q0]), "operationType" : NewBodyOperationType.ADD, "endBound" : BoundingType.SYMMETRIC, "depth" : 3.5 * mm});
        }
        {
            var Q0;
            {var subQ0=sQuery(id+"F0.wireOp",EDGE,"E14");var subQ1=sQuery(id+"F0.wireOp",EDGE,"E13");Q0=makeQuery(id+"F1.opExtrude","SWEPT_EDGE",EDGE,{"disambiguationData":[OSD([subQ1,subQ0]),TDD([makeQuery(id+"F0.imprint","INTERSECT",VERTEX,{"disambiguationData":[OD(1.0)],"derivedFrom":[subQ1,subQ0]})])]});}
            var Q1;
            {var subQ0=sQuery(id+"F0.wireOp",EDGE,"E14");var subQ1=sQuery(id+"F0.wireOp",EDGE,"E13");Q1=makeQuery(id+"F1.opExtrude","SWEPT_EDGE",EDGE,{"disambiguationData":[OSD([subQ1,subQ0]),TDD([makeQuery(id+"F0.imprint","INTERSECT",VERTEX,{"disambiguationData":[OD(0.0)],"derivedFrom":[subQ1,subQ0]})])]});}
            fillet(context, id + "F3", {"entities" : qUnion([Q0, Q1]), "radius" : 5.08 * mm, "tangentPropagation" : true, "allowEdgeOverflow" : false});
        }
        {
            var Q0;
            Q0=makeQuery(id+"F1.opExtrude","CAP_FACE",FACE,{"disambiguationData":[OSD([sQuery(id+"F0.wireOp",EDGE,"E11"),sQuery(id+"F0.wireOp",EDGE,"E12.1.0"),sQuery(id+"F0.wireOp",EDGE,"E12.2.0"),sQuery(id+"F0.wireOp",EDGE,"E12.3.0"),sQuery(id+"F0.wireOp",EDGE,"E12.4.0"),sQuery(id+"F0.wireOp",EDGE,"E13"),sQuery(id+"F0.wireOp",EDGE,"E14"),sQuery(id+"F0.wireOp",EDGE,"E15")])],"isStart":false});
            var sketch = newSketch(context, id + "F4", { "sketchPlane" : qUnion([Q0])});
            skLineSegment(sketch, "E16", {"start": v(69.07, 11.87) * mm, "end": v(84.2, 14.47) * mm});
            skLineSegment(sketch, "E17", {"start": v(48.72, -50.37) * mm, "end": v(59.4, -61.4) * mm});
            skArc(sketch, "E18", {"start": v(48.72, -50.37) * mm, "mid": v(52.15, -46.82) * mm, "end": v(55.31, -43.03) * mm});
            skArc(sketch, "E19", {"start": v(59.4, -61.4) * mm, "mid": v(63.57, -57.07) * mm, "end": v(67.42, -52.46) * mm});
            skLineSegment(sketch, "E20", {"start": v(70.04, 2.3) * mm, "end": v(85.38, 2.81) * mm});
            skLineSegment(sketch, "E21", {"start": v(70.08, 0.47) * mm, "end": v(85.42, 0.57) * mm});
            skLineSegment(sketch, "E22", {"start": v(69.45, -9.37) * mm, "end": v(84.66, -11.42) * mm});
            skLineSegment(sketch, "E23", {"start": v(69.18, -11.18) * mm, "end": v(84.33, -13.63) * mm});
            skArc(sketch, "E24.trimOffspring", {"start": v(69.45, -9.37) * mm, "mid": v(69.94, -4.46) * mm, "end": v(70.08, 0.47) * mm});
            skArc(sketch, "E25.trimOffspring", {"start": v(70.04, 2.3) * mm, "mid": v(69.72, 7.1) * mm, "end": v(69.07, 11.87) * mm});
            skArc(sketch, "E26.trimOffspring", {"start": v(84.66, -11.42) * mm, "mid": v(85.25, -5.44) * mm, "end": v(85.42, 0.57) * mm});
            skArc(sketch, "E27.trimOffspring", {"start": v(85.38, 2.81) * mm, "mid": v(84.99, 8.66) * mm, "end": v(84.2, 14.47) * mm});
            skLineSegment(sketch, "E28", {"start": v(66.93, -20.78) * mm, "end": v(81.58, -25.33) * mm});
            skLineSegment(sketch, "E29", {"start": v(66.36, -22.53) * mm, "end": v(80.9, -27.46) * mm});
            skArc(sketch, "E30.trimOffspring", {"start": v(66.93, -20.78) * mm, "mid": v(68.22, -16.02) * mm, "end": v(69.18, -11.18) * mm});
            skArc(sketch, "E31.trimOffspring", {"start": v(81.58, -25.33) * mm, "mid": v(83.16, -19.53) * mm, "end": v(84.33, -13.63) * mm});
            skLineSegment(sketch, "E32", {"start": v(62.54, -31.61) * mm, "end": v(76.24, -38.54) * mm});
            skLineSegment(sketch, "E33", {"start": v(61.7, -33.24) * mm, "end": v(75.2, -40.52) * mm});
            skArc(sketch, "E34.trimOffspring", {"start": v(62.54, -31.61) * mm, "mid": v(64.61, -27.14) * mm, "end": v(66.36, -22.53) * mm});
            skArc(sketch, "E35.trimOffspring", {"start": v(76.24, -38.54) * mm, "mid": v(78.76, -33.08) * mm, "end": v(80.9, -27.46) * mm});
            skLineSegment(sketch, "E36", {"start": v(56.42, -41.57) * mm, "end": v(68.77, -50.67) * mm});
            skLineSegment(sketch, "E37", {"start": v(55.31, -43.03) * mm, "end": v(67.42, -52.46) * mm});
            skArc(sketch, "E38.trimOffspring", {"start": v(68.77, -50.67) * mm, "mid": v(72.17, -45.7) * mm, "end": v(75.2, -40.52) * mm});
            skArc(sketch, "E39.trimOffspring", {"start": v(56.42, -41.57) * mm, "mid": v(59.2, -37.5) * mm, "end": v(61.7, -33.24) * mm});
            skArc(sketch, "E40.1.0", {"start": v(30.37, 63.16) * mm, "mid": v(25.85, 65.14) * mm, "end": v(21.2, 66.8) * mm});
            skArc(sketch, "E40.1.1", {"start": v(37.02, 76.99) * mm, "mid": v(31.51, 79.4) * mm, "end": v(25.85, 81.42) * mm});
            skLineSegment(sketch, "E40.1.2", {"start": v(30.37, 63.16) * mm, "end": v(37.02, 76.99) * mm});
            skLineSegment(sketch, "E40.1.3", {"start": v(50.68, 48.4) * mm, "end": v(61.78, 59) * mm});
            skArc(sketch, "E40.1.4", {"start": v(23.71, 82.07) * mm, "mid": v(18.03, 83.5) * mm, "end": v(12.26, 84.54) * mm});
            skLineSegment(sketch, "E40.1.5", {"start": v(41.93, 56.15) * mm, "end": v(51.11, 68.45) * mm});
            skLineSegment(sketch, "E40.1.6", {"start": v(40.45, 57.23) * mm, "end": v(49.3, 69.76) * mm});
            skLineSegment(sketch, "E40.1.7", {"start": v(10.05, 69.35) * mm, "end": v(12.26, 84.54) * mm});
            skLineSegment(sketch, "E40.1.8", {"start": v(19.45, 67.33) * mm, "end": v(23.71, 82.07) * mm});
            skArc(sketch, "E40.1.9", {"start": v(62.96, 30.77) * mm, "mid": v(60.64, 35.13) * mm, "end": v(58.02, 39.3) * mm});
            skArc(sketch, "E40.1.10", {"start": v(49.3, 69.76) * mm, "mid": v(44.27, 73.06) * mm, "end": v(39.02, 76) * mm});
            skLineSegment(sketch, "E40.1.11", {"start": v(56.97, 40.81) * mm, "end": v(69.44, 49.75) * mm});
            skArc(sketch, "E40.1.12", {"start": v(60.21, 60.6) * mm, "mid": v(55.8, 64.68) * mm, "end": v(51.11, 68.45) * mm});
            skLineSegment(sketch, "E40.1.13", {"start": v(49.4, 49.71) * mm, "end": v(60.21, 60.6) * mm});
            skLineSegment(sketch, "E40.1.14", {"start": v(62.96, 30.77) * mm, "end": v(76.75, 37.51) * mm});
            skLineSegment(sketch, "E40.1.15", {"start": v(21.2, 66.8) * mm, "end": v(25.85, 81.42) * mm});
            skLineSegment(sketch, "E40.1.16", {"start": v(32.01, 62.34) * mm, "end": v(39.02, 76) * mm});
            skLineSegment(sketch, "E40.1.17", {"start": v(58.02, 39.3) * mm, "end": v(70.72, 47.91) * mm});
            skArc(sketch, "E40.1.18", {"start": v(19.45, 67.33) * mm, "mid": v(14.79, 68.5) * mm, "end": v(10.05, 69.35) * mm});
            skArc(sketch, "E40.1.19", {"start": v(49.4, 49.71) * mm, "mid": v(45.78, 53.06) * mm, "end": v(41.93, 56.15) * mm});
            skArc(sketch, "E40.1.20", {"start": v(69.44, 49.75) * mm, "mid": v(65.77, 54.51) * mm, "end": v(61.78, 59) * mm});
            skArc(sketch, "E40.1.21", {"start": v(40.45, 57.23) * mm, "mid": v(36.32, 59.93) * mm, "end": v(32.01, 62.34) * mm});
            skArc(sketch, "E40.1.22", {"start": v(76.75, 37.51) * mm, "mid": v(73.92, 42.82) * mm, "end": v(70.72, 47.91) * mm});
            skArc(sketch, "E40.1.23", {"start": v(56.97, 40.81) * mm, "mid": v(53.96, 44.72) * mm, "end": v(50.68, 48.4) * mm});
            skArc(sketch, "E40.2.0", {"start": v(-50.68, 48.4) * mm, "mid": v(-53.96, 44.72) * mm, "end": v(-56.97, 40.8) * mm});
            skArc(sketch, "E40.2.1", {"start": v(-61.78, 59) * mm, "mid": v(-65.78, 54.5) * mm, "end": v(-69.45, 49.75) * mm});
            skLineSegment(sketch, "E40.2.2", {"start": v(-50.68, 48.4) * mm, "end": v(-61.78, 59) * mm});
            skLineSegment(sketch, "E40.2.3", {"start": v(-30.37, 63.16) * mm, "end": v(-37.02, 76.99) * mm});
            skArc(sketch, "E40.2.4", {"start": v(-70.73, 47.91) * mm, "mid": v(-73.84, 42.95) * mm, "end": v(-76.62, 37.78) * mm});
            skLineSegment(sketch, "E40.2.5", {"start": v(-40.45, 57.23) * mm, "end": v(-49.3, 69.76) * mm});
            skLineSegment(sketch, "E40.2.6", {"start": v(-41.93, 56.15) * mm, "end": v(-51.11, 68.45) * mm});
            skLineSegment(sketch, "E40.2.7", {"start": v(-62.85, 31) * mm, "end": v(-76.62, 37.78) * mm});
            skLineSegment(sketch, "E40.2.8", {"start": v(-58.02, 39.3) * mm, "end": v(-70.73, 47.91) * mm});
            skArc(sketch, "E40.2.9", {"start": v(-9.81, 69.39) * mm, "mid": v(-14.67, 68.53) * mm, "end": v(-19.45, 67.33) * mm});
            skArc(sketch, "E40.2.10", {"start": v(-51.11, 68.45) * mm, "mid": v(-55.8, 64.68) * mm, "end": v(-60.21, 60.6) * mm});
            skLineSegment(sketch, "E40.2.11", {"start": v(-21.21, 66.8) * mm, "end": v(-25.85, 81.42) * mm});
            skArc(sketch, "E40.2.12", {"start": v(-39.03, 75.99) * mm, "mid": v(-44.28, 73.06) * mm, "end": v(-49.3, 69.76) * mm});
            skLineSegment(sketch, "E40.2.13", {"start": v(-32.02, 62.34) * mm, "end": v(-39.03, 75.99) * mm});
            skLineSegment(sketch, "E40.2.14", {"start": v(-9.81, 69.39) * mm, "end": v(-11.96, 84.58) * mm});
            skLineSegment(sketch, "E40.2.15", {"start": v(-56.97, 40.8) * mm, "end": v(-69.45, 49.75) * mm});
            skLineSegment(sketch, "E40.2.16", {"start": v(-49.4, 49.71) * mm, "end": v(-60.21, 60.6) * mm});
            skLineSegment(sketch, "E40.2.17", {"start": v(-19.45, 67.33) * mm, "end": v(-23.71, 82.07) * mm});
            skArc(sketch, "E40.2.18", {"start": v(-58.02, 39.3) * mm, "mid": v(-60.58, 35.23) * mm, "end": v(-62.85, 31) * mm});
            skArc(sketch, "E40.2.19", {"start": v(-32.02, 62.34) * mm, "mid": v(-36.32, 59.93) * mm, "end": v(-40.45, 57.23) * mm});
            skArc(sketch, "E40.2.20", {"start": v(-25.85, 81.42) * mm, "mid": v(-31.52, 79.4) * mm, "end": v(-37.02, 76.99) * mm});
            skArc(sketch, "E40.2.21", {"start": v(-41.93, 56.15) * mm, "mid": v(-45.78, 53.06) * mm, "end": v(-49.4, 49.71) * mm});
            skArc(sketch, "E40.2.22", {"start": v(-11.96, 84.58) * mm, "mid": v(-17.88, 83.53) * mm, "end": v(-23.71, 82.07) * mm});
            skArc(sketch, "E40.2.23", {"start": v(-21.21, 66.8) * mm, "mid": v(-25.86, 65.14) * mm, "end": v(-30.37, 63.16) * mm});
            skArc(sketch, "E40.3.0", {"start": v(-61.7, -33.24) * mm, "mid": v(-59.2, -37.5) * mm, "end": v(-56.42, -41.57) * mm});
            skArc(sketch, "E40.3.1", {"start": v(-75.2, -40.52) * mm, "mid": v(-72.17, -45.71) * mm, "end": v(-68.77, -50.68) * mm});
            skLineSegment(sketch, "E40.3.2", {"start": v(-61.7, -33.24) * mm, "end": v(-75.2, -40.52) * mm});
            skLineSegment(sketch, "E40.3.3", {"start": v(-69.45, -9.37) * mm, "end": v(-84.66, -11.42) * mm});
            skArc(sketch, "E40.3.4", {"start": v(-67.42, -52.46) * mm, "mid": v(-63.66, -56.96) * mm, "end": v(-59.6, -61.2) * mm});
            skLineSegment(sketch, "E40.3.5", {"start": v(-66.93, -20.78) * mm, "end": v(-81.58, -25.33) * mm});
            skLineSegment(sketch, "E40.3.6", {"start": v(-66.36, -22.53) * mm, "end": v(-80.9, -27.46) * mm});
            skLineSegment(sketch, "E40.3.7", {"start": v(-48.9, -50.2) * mm, "end": v(-59.6, -61.2) * mm});
            skLineSegment(sketch, "E40.3.8", {"start": v(-55.31, -43.03) * mm, "end": v(-67.42, -52.46) * mm});
            skArc(sketch, "E40.3.9", {"start": v(-69.03, 12.11) * mm, "mid": v(-69.7, 7.22) * mm, "end": v(-70.04, 2.3) * mm});
            skArc(sketch, "E40.3.10", {"start": v(-80.9, -27.46) * mm, "mid": v(-78.76, -33.08) * mm, "end": v(-76.24, -38.54) * mm});
            skLineSegment(sketch, "E40.3.11", {"start": v(-70.08, 0.47) * mm, "end": v(-85.42, 0.57) * mm});
            skArc(sketch, "E40.3.12", {"start": v(-84.33, -13.63) * mm, "mid": v(-83.16, -19.53) * mm, "end": v(-81.58, -25.33) * mm});
            skLineSegment(sketch, "E40.3.13", {"start": v(-69.18, -11.19) * mm, "end": v(-84.33, -13.63) * mm});
            skLineSegment(sketch, "E40.3.14", {"start": v(-69.03, 12.11) * mm, "end": v(-84.14, 14.76) * mm});
            skLineSegment(sketch, "E40.3.15", {"start": v(-56.42, -41.57) * mm, "end": v(-68.77, -50.68) * mm});
            skLineSegment(sketch, "E40.3.16", {"start": v(-62.54, -31.62) * mm, "end": v(-76.24, -38.54) * mm});
            skLineSegment(sketch, "E40.3.17", {"start": v(-70.04, 2.3) * mm, "end": v(-85.38, 2.8) * mm});
            skArc(sketch, "E40.3.18", {"start": v(-55.31, -43.03) * mm, "mid": v(-52.23, -46.73) * mm, "end": v(-48.9, -50.2) * mm});
            skArc(sketch, "E40.3.19", {"start": v(-69.18, -11.19) * mm, "mid": v(-68.22, -16.02) * mm, "end": v(-66.93, -20.78) * mm});
            skArc(sketch, "E40.3.20", {"start": v(-85.42, 0.57) * mm, "mid": v(-85.25, -5.44) * mm, "end": v(-84.66, -11.42) * mm});
            skArc(sketch, "E40.3.21", {"start": v(-66.36, -22.53) * mm, "mid": v(-64.61, -27.14) * mm, "end": v(-62.54, -31.62) * mm});
            skArc(sketch, "E40.3.22", {"start": v(-84.14, 14.76) * mm, "mid": v(-84.97, 8.8) * mm, "end": v(-85.38, 2.8) * mm});
            skArc(sketch, "E40.3.23", {"start": v(-70.08, 0.47) * mm, "mid": v(-69.94, -4.46) * mm, "end": v(-69.45, -9.37) * mm});
            skSolve(sketch);
        }
        {
            var Q0;
            Q0=makeQuery(id+"F4.imprint","IMPRINT",FACE,{"disambiguationData":[TD([[makeQuery(id+"F4.imprint","IMPRINT",EDGE,{"derivedFrom":sQuery(id+"F4.wireOp",EDGE,"E40.3.4")}),1.0]])]});
            var Q1;
            Q1=makeQuery(id+"F4.imprint","IMPRINT",FACE,{"disambiguationData":[TD([[makeQuery(id+"F4.imprint","IMPRINT",EDGE,{"derivedFrom":sQuery(id+"F4.wireOp",EDGE,"E40.3.0")}),-1.0]])]});
            var Q2;
            Q2=makeQuery(id+"F4.imprint","IMPRINT",FACE,{"disambiguationData":[TD([[makeQuery(id+"F4.imprint","IMPRINT",EDGE,{"derivedFrom":sQuery(id+"F4.wireOp",EDGE,"E40.2.4")}),1.0]])]});
            var Q3;
            Q3=makeQuery(id+"F4.imprint","IMPRINT",FACE,{"disambiguationData":[TD([[makeQuery(id+"F4.imprint","IMPRINT",EDGE,{"derivedFrom":sQuery(id+"F4.wireOp",EDGE,"E40.2.0")}),-1.0]])]});
            var Q4;
            Q4=makeQuery(id+"F4.imprint","IMPRINT",FACE,{"disambiguationData":[TD([[makeQuery(id+"F4.imprint","IMPRINT",EDGE,{"derivedFrom":sQuery(id+"F4.wireOp",EDGE,"E40.1.4")}),1.0]])]});
            var Q5;
            Q5=makeQuery(id+"F4.imprint","IMPRINT",FACE,{"disambiguationData":[TD([[makeQuery(id+"F4.imprint","IMPRINT",EDGE,{"derivedFrom":sQuery(id+"F4.wireOp",EDGE,"E40.1.0")}),-1.0]])]});
            var Q6;
            Q6=makeQuery(id+"F4.imprint","IMPRINT",FACE,{"disambiguationData":[TD([[makeQuery(id+"F4.imprint","IMPRINT",EDGE,{"derivedFrom":sQuery(id+"F4.wireOp",EDGE,"E16")}),-1.0]])]});
            var Q7;
            Q7=makeQuery(id+"F4.imprint","IMPRINT",FACE,{"disambiguationData":[TD([[makeQuery(id+"F4.imprint","IMPRINT",EDGE,{"derivedFrom":sQuery(id+"F4.wireOp",EDGE,"E21")}),-1.0]])]});
            extrude(context, id + "F5", {"entities" : qUnion([Q0, Q1, Q2, Q3, Q4, Q5, Q6, Q7]), "operationType" : NewBodyOperationType.REMOVE, "oppositeDirection" : true, "depth" : 4.5 * mm});
        }
        {
            var Q0;
            Q0=makeQuery(id+"F4.imprint","IMPRINT",FACE,{"disambiguationData":[TD([[makeQuery(id+"F4.imprint","IMPRINT",EDGE,{"derivedFrom":sQuery(id+"F4.wireOp",EDGE,"E40.3.6")}),1.0]])]});
            var Q1;
            Q1=makeQuery(id+"F4.imprint","IMPRINT",FACE,{"disambiguationData":[TD([[makeQuery(id+"F4.imprint","IMPRINT",EDGE,{"derivedFrom":sQuery(id+"F4.wireOp",EDGE,"E40.3.5")}),-1.0]])]});
            var Q2;
            Q2=makeQuery(id+"F4.imprint","IMPRINT",FACE,{"disambiguationData":[TD([[makeQuery(id+"F4.imprint","IMPRINT",EDGE,{"derivedFrom":sQuery(id+"F4.wireOp",EDGE,"E40.3.3")}),-1.0]])]});
            var Q3;
            Q3=makeQuery(id+"F4.imprint","IMPRINT",FACE,{"disambiguationData":[TD([[makeQuery(id+"F4.imprint","IMPRINT",EDGE,{"derivedFrom":sQuery(id+"F4.wireOp",EDGE,"E40.3.9")}),-1.0]])]});
            var Q4;
            Q4=makeQuery(id+"F4.imprint","IMPRINT",FACE,{"disambiguationData":[TD([[makeQuery(id+"F4.imprint","IMPRINT",EDGE,{"derivedFrom":sQuery(id+"F4.wireOp",EDGE,"E40.2.6")}),1.0]])]});
            var Q5;
            Q5=makeQuery(id+"F4.imprint","IMPRINT",FACE,{"disambiguationData":[TD([[makeQuery(id+"F4.imprint","IMPRINT",EDGE,{"derivedFrom":sQuery(id+"F4.wireOp",EDGE,"E40.2.5")}),-1.0]])]});
            var Q6;
            Q6=makeQuery(id+"F4.imprint","IMPRINT",FACE,{"disambiguationData":[TD([[makeQuery(id+"F4.imprint","IMPRINT",EDGE,{"derivedFrom":sQuery(id+"F4.wireOp",EDGE,"E40.2.3")}),-1.0]])]});
            var Q7;
            Q7=makeQuery(id+"F4.imprint","IMPRINT",FACE,{"disambiguationData":[TD([[makeQuery(id+"F4.imprint","IMPRINT",EDGE,{"derivedFrom":sQuery(id+"F4.wireOp",EDGE,"E40.2.9")}),-1.0]])]});
            var Q8;
            Q8=makeQuery(id+"F4.imprint","IMPRINT",FACE,{"disambiguationData":[TD([[makeQuery(id+"F4.imprint","IMPRINT",EDGE,{"derivedFrom":sQuery(id+"F4.wireOp",EDGE,"E40.1.6")}),1.0]])]});
            var Q9;
            Q9=makeQuery(id+"F4.imprint","IMPRINT",FACE,{"disambiguationData":[TD([[makeQuery(id+"F4.imprint","IMPRINT",EDGE,{"derivedFrom":sQuery(id+"F4.wireOp",EDGE,"E40.1.5")}),-1.0]])]});
            var Q10;
            Q10=makeQuery(id+"F4.imprint","IMPRINT",FACE,{"disambiguationData":[TD([[makeQuery(id+"F4.imprint","IMPRINT",EDGE,{"derivedFrom":sQuery(id+"F4.wireOp",EDGE,"E40.1.3")}),-1.0]])]});
            var Q11;
            Q11=makeQuery(id+"F4.imprint","IMPRINT",FACE,{"disambiguationData":[TD([[makeQuery(id+"F4.imprint","IMPRINT",EDGE,{"derivedFrom":sQuery(id+"F4.wireOp",EDGE,"E40.1.9")}),-1.0]])]});
            var Q12;
            Q12=makeQuery(id+"F4.imprint","IMPRINT",FACE,{"disambiguationData":[TD([[makeQuery(id+"F4.imprint","IMPRINT",EDGE,{"derivedFrom":sQuery(id+"F4.wireOp",EDGE,"E23")}),-1.0]])]});
            var Q13;
            Q13=makeQuery(id+"F4.imprint","IMPRINT",FACE,{"disambiguationData":[TD([[makeQuery(id+"F4.imprint","IMPRINT",EDGE,{"derivedFrom":sQuery(id+"F4.wireOp",EDGE,"E29")}),-1.0]])]});
            var Q14;
            Q14=makeQuery(id+"F4.imprint","IMPRINT",FACE,{"disambiguationData":[TD([[makeQuery(id+"F4.imprint","IMPRINT",EDGE,{"derivedFrom":sQuery(id+"F4.wireOp",EDGE,"E33")}),-1.0]])]});
            var Q15;
            Q15=makeQuery(id+"F4.imprint","IMPRINT",FACE,{"disambiguationData":[TD([[makeQuery(id+"F4.imprint","IMPRINT",EDGE,{"derivedFrom":sQuery(id+"F4.wireOp",EDGE,"E17")}),1.0]])]});
            extrude(context, id + "F6", {"entities" : qUnion([Q0, Q1, Q2, Q3, Q4, Q5, Q6, Q7, Q8, Q9, Q10, Q11, Q12, Q13, Q14, Q15]), "operationType" : NewBodyOperationType.REMOVE, "oppositeDirection" : true, "depth" : 2.5 * mm});
        }
        {
            var Q0;
            Q0=makeQuery(id+"F5.boolean.opBoolean","COPY",EDGE,{"derivedFrom":makeQuery(id+"F5.opExtrude","SWEPT_EDGE",EDGE,{"disambiguationData":[OSD([sQuery(id+"F4.wireOp",EDGE,"E40.3.8"),sQuery(id+"F4.wireOp",EDGE,"E40.3.18")])]})});
            var Q1;
            Q1=makeQuery(id+"F5.boolean.opBoolean","COPY",EDGE,{"derivedFrom":makeQuery(id+"F5.opExtrude","SWEPT_EDGE",EDGE,{"disambiguationData":[OSD([sQuery(id+"F4.wireOp",EDGE,"E40.3.0"),sQuery(id+"F4.wireOp",EDGE,"E40.3.2")])]})});
            var Q2;
            Q2=makeQuery(id+"F6.boolean.opBoolean","COPY",EDGE,{"derivedFrom":makeQuery(id+"F6.opExtrude","SWEPT_EDGE",EDGE,{"disambiguationData":[OSD([sQuery(id+"F4.wireOp",EDGE,"E40.3.6"),sQuery(id+"F4.wireOp",EDGE,"E40.3.21")])]})});
            var Q3;
            Q3=makeQuery(id+"F6.boolean.opBoolean","COPY",EDGE,{"derivedFrom":makeQuery(id+"F6.opExtrude","SWEPT_EDGE",EDGE,{"disambiguationData":[OSD([sQuery(id+"F4.wireOp",EDGE,"E40.3.13"),sQuery(id+"F4.wireOp",EDGE,"E40.3.19")])]})});
            var Q4;
            Q4=makeQuery(id+"F6.boolean.opBoolean","COPY",EDGE,{"derivedFrom":makeQuery(id+"F6.opExtrude","SWEPT_EDGE",EDGE,{"disambiguationData":[OSD([sQuery(id+"F4.wireOp",EDGE,"E40.3.9"),sQuery(id+"F4.wireOp",EDGE,"E40.3.14")])]})});
            var Q5;
            Q5=makeQuery(id+"F6.boolean.opBoolean","COPY",EDGE,{"derivedFrom":makeQuery(id+"F6.opExtrude","SWEPT_EDGE",EDGE,{"disambiguationData":[OSD([sQuery(id+"F4.wireOp",EDGE,"E40.3.11"),sQuery(id+"F4.wireOp",EDGE,"E40.3.23")])]})});
            var Q6;
            Q6=makeQuery(id+"F6.boolean.opBoolean","COPY",EDGE,{"derivedFrom":makeQuery(id+"F6.opExtrude","SWEPT_EDGE",EDGE,{"disambiguationData":[OSD([sQuery(id+"F4.wireOp",EDGE,"E40.3.14"),sQuery(id+"F4.wireOp",EDGE,"E40.3.22")])]})});
            var Q7;
            Q7=makeQuery(id+"F6.boolean.opBoolean","COPY",EDGE,{"derivedFrom":makeQuery(id+"F6.opExtrude","SWEPT_EDGE",EDGE,{"disambiguationData":[OSD([sQuery(id+"F4.wireOp",EDGE,"E40.3.11"),sQuery(id+"F4.wireOp",EDGE,"E40.3.20")])]})});
            var Q8;
            Q8=makeQuery(id+"F6.boolean.opBoolean","COPY",EDGE,{"derivedFrom":makeQuery(id+"F6.opExtrude","SWEPT_EDGE",EDGE,{"disambiguationData":[OSD([sQuery(id+"F4.wireOp",EDGE,"E40.3.12"),sQuery(id+"F4.wireOp",EDGE,"E40.3.13")])]})});
            var Q9;
            Q9=makeQuery(id+"F6.boolean.opBoolean","COPY",EDGE,{"derivedFrom":makeQuery(id+"F6.opExtrude","SWEPT_EDGE",EDGE,{"disambiguationData":[OSD([sQuery(id+"F4.wireOp",EDGE,"E40.3.6"),sQuery(id+"F4.wireOp",EDGE,"E40.3.10")])]})});
            var Q10;
            Q10=makeQuery(id+"F5.boolean.opBoolean","COPY",EDGE,{"derivedFrom":makeQuery(id+"F5.opExtrude","SWEPT_EDGE",EDGE,{"disambiguationData":[OSD([sQuery(id+"F4.wireOp",EDGE,"E40.3.1"),sQuery(id+"F4.wireOp",EDGE,"E40.3.2")])]})});
            var Q11;
            Q11=makeQuery(id+"F5.boolean.opBoolean","COPY",EDGE,{"derivedFrom":makeQuery(id+"F5.opExtrude","SWEPT_EDGE",EDGE,{"disambiguationData":[OSD([sQuery(id+"F4.wireOp",EDGE,"E40.3.4"),sQuery(id+"F4.wireOp",EDGE,"E40.3.8")])]})});
            var Q12;
            Q12=makeQuery(id+"F5.boolean.opBoolean","COPY",EDGE,{"derivedFrom":makeQuery(id+"F5.opExtrude","SWEPT_EDGE",EDGE,{"disambiguationData":[OSD([sQuery(id+"F4.wireOp",EDGE,"E40.3.4"),sQuery(id+"F4.wireOp",EDGE,"E40.3.7")])]})});
            var Q13;
            Q13=makeQuery(id+"F5.boolean.opBoolean","COPY",EDGE,{"derivedFrom":makeQuery(id+"F5.opExtrude","SWEPT_EDGE",EDGE,{"disambiguationData":[OSD([sQuery(id+"F4.wireOp",EDGE,"E40.3.1"),sQuery(id+"F4.wireOp",EDGE,"E40.3.15")])]})});
            var Q14;
            Q14=makeQuery(id+"F6.boolean.opBoolean","COPY",EDGE,{"derivedFrom":makeQuery(id+"F6.opExtrude","SWEPT_EDGE",EDGE,{"disambiguationData":[OSD([sQuery(id+"F4.wireOp",EDGE,"E40.3.10"),sQuery(id+"F4.wireOp",EDGE,"E40.3.16")])]})});
            var Q15;
            Q15=makeQuery(id+"F6.boolean.opBoolean","COPY",EDGE,{"derivedFrom":makeQuery(id+"F6.opExtrude","SWEPT_EDGE",EDGE,{"disambiguationData":[OSD([sQuery(id+"F4.wireOp",EDGE,"E40.3.5"),sQuery(id+"F4.wireOp",EDGE,"E40.3.12")])]})});
            var Q16;
            Q16=makeQuery(id+"F6.boolean.opBoolean","COPY",EDGE,{"derivedFrom":makeQuery(id+"F6.opExtrude","SWEPT_EDGE",EDGE,{"disambiguationData":[OSD([sQuery(id+"F4.wireOp",EDGE,"E40.3.17"),sQuery(id+"F4.wireOp",EDGE,"E40.3.22")])]})});
            var Q17;
            Q17=makeQuery(id+"F6.boolean.opBoolean","COPY",EDGE,{"derivedFrom":makeQuery(id+"F6.opExtrude","SWEPT_EDGE",EDGE,{"disambiguationData":[OSD([sQuery(id+"F4.wireOp",EDGE,"E40.3.3"),sQuery(id+"F4.wireOp",EDGE,"E40.3.20")])]})});
            var Q18;
            Q18=makeQuery(id+"F5.boolean.opBoolean","COPY",EDGE,{"derivedFrom":makeQuery(id+"F5.opExtrude","SWEPT_EDGE",EDGE,{"disambiguationData":[OSD([sQuery(id+"F4.wireOp",EDGE,"E40.3.7"),sQuery(id+"F4.wireOp",EDGE,"E40.3.18")])]})});
            var Q19;
            Q19=makeQuery(id+"F5.boolean.opBoolean","COPY",EDGE,{"derivedFrom":makeQuery(id+"F5.opExtrude","SWEPT_EDGE",EDGE,{"disambiguationData":[OSD([sQuery(id+"F4.wireOp",EDGE,"E40.3.0"),sQuery(id+"F4.wireOp",EDGE,"E40.3.15")])]})});
            var Q20;
            Q20=makeQuery(id+"F6.boolean.opBoolean","COPY",EDGE,{"derivedFrom":makeQuery(id+"F6.opExtrude","SWEPT_EDGE",EDGE,{"disambiguationData":[OSD([sQuery(id+"F4.wireOp",EDGE,"E40.3.16"),sQuery(id+"F4.wireOp",EDGE,"E40.3.21")])]})});
            var Q21;
            Q21=makeQuery(id+"F6.boolean.opBoolean","COPY",EDGE,{"derivedFrom":makeQuery(id+"F6.opExtrude","SWEPT_EDGE",EDGE,{"disambiguationData":[OSD([sQuery(id+"F4.wireOp",EDGE,"E40.3.5"),sQuery(id+"F4.wireOp",EDGE,"E40.3.19")])]})});
            var Q22;
            Q22=makeQuery(id+"F6.boolean.opBoolean","COPY",EDGE,{"derivedFrom":makeQuery(id+"F6.opExtrude","SWEPT_EDGE",EDGE,{"disambiguationData":[OSD([sQuery(id+"F4.wireOp",EDGE,"E40.3.3"),sQuery(id+"F4.wireOp",EDGE,"E40.3.23")])]})});
            var Q23;
            Q23=makeQuery(id+"F6.boolean.opBoolean","COPY",EDGE,{"derivedFrom":makeQuery(id+"F6.opExtrude","SWEPT_EDGE",EDGE,{"disambiguationData":[OSD([sQuery(id+"F4.wireOp",EDGE,"E40.3.9"),sQuery(id+"F4.wireOp",EDGE,"E40.3.17")])]})});
            var Q24;
            Q24=makeQuery(id+"F5.boolean.opBoolean","COPY",EDGE,{"derivedFrom":makeQuery(id+"F5.opExtrude","SWEPT_EDGE",EDGE,{"disambiguationData":[OSD([sQuery(id+"F4.wireOp",EDGE,"E40.2.7"),sQuery(id+"F4.wireOp",EDGE,"E40.2.18")])]})});
            var Q25;
            Q25=makeQuery(id+"F5.boolean.opBoolean","COPY",EDGE,{"derivedFrom":makeQuery(id+"F5.opExtrude","SWEPT_EDGE",EDGE,{"disambiguationData":[OSD([sQuery(id+"F4.wireOp",EDGE,"E40.2.0"),sQuery(id+"F4.wireOp",EDGE,"E40.2.15")])]})});
            var Q26;
            Q26=makeQuery(id+"F6.boolean.opBoolean","COPY",EDGE,{"derivedFrom":makeQuery(id+"F6.opExtrude","SWEPT_EDGE",EDGE,{"disambiguationData":[OSD([sQuery(id+"F4.wireOp",EDGE,"E40.2.16"),sQuery(id+"F4.wireOp",EDGE,"E40.2.21")])]})});
            var Q27;
            Q27=makeQuery(id+"F6.boolean.opBoolean","COPY",EDGE,{"derivedFrom":makeQuery(id+"F6.opExtrude","SWEPT_EDGE",EDGE,{"disambiguationData":[OSD([sQuery(id+"F4.wireOp",EDGE,"E40.2.5"),sQuery(id+"F4.wireOp",EDGE,"E40.2.19")])]})});
            var Q28;
            Q28=makeQuery(id+"F6.boolean.opBoolean","COPY",EDGE,{"derivedFrom":makeQuery(id+"F6.opExtrude","SWEPT_EDGE",EDGE,{"disambiguationData":[OSD([sQuery(id+"F4.wireOp",EDGE,"E40.2.3"),sQuery(id+"F4.wireOp",EDGE,"E40.2.23")])]})});
            var Q29;
            Q29=makeQuery(id+"F6.boolean.opBoolean","COPY",EDGE,{"derivedFrom":makeQuery(id+"F6.opExtrude","SWEPT_EDGE",EDGE,{"disambiguationData":[OSD([sQuery(id+"F4.wireOp",EDGE,"E40.2.9"),sQuery(id+"F4.wireOp",EDGE,"E40.2.17")])]})});
            var Q30;
            Q30=makeQuery(id+"F5.boolean.opBoolean","COPY",EDGE,{"derivedFrom":makeQuery(id+"F5.opExtrude","SWEPT_EDGE",EDGE,{"disambiguationData":[OSD([sQuery(id+"F4.wireOp",EDGE,"E40.2.8"),sQuery(id+"F4.wireOp",EDGE,"E40.2.18")])]})});
            var Q31;
            Q31=makeQuery(id+"F5.boolean.opBoolean","COPY",EDGE,{"derivedFrom":makeQuery(id+"F5.opExtrude","SWEPT_EDGE",EDGE,{"disambiguationData":[OSD([sQuery(id+"F4.wireOp",EDGE,"E40.2.0"),sQuery(id+"F4.wireOp",EDGE,"E40.2.2")])]})});
            var Q32;
            Q32=makeQuery(id+"F6.boolean.opBoolean","COPY",EDGE,{"derivedFrom":makeQuery(id+"F6.opExtrude","SWEPT_EDGE",EDGE,{"disambiguationData":[OSD([sQuery(id+"F4.wireOp",EDGE,"E40.2.6"),sQuery(id+"F4.wireOp",EDGE,"E40.2.21")])]})});
            var Q33;
            Q33=makeQuery(id+"F6.boolean.opBoolean","COPY",EDGE,{"derivedFrom":makeQuery(id+"F6.opExtrude","SWEPT_EDGE",EDGE,{"disambiguationData":[OSD([sQuery(id+"F4.wireOp",EDGE,"E40.2.13"),sQuery(id+"F4.wireOp",EDGE,"E40.2.19")])]})});
            var Q34;
            Q34=makeQuery(id+"F6.boolean.opBoolean","COPY",EDGE,{"derivedFrom":makeQuery(id+"F6.opExtrude","SWEPT_EDGE",EDGE,{"disambiguationData":[OSD([sQuery(id+"F4.wireOp",EDGE,"E40.2.11"),sQuery(id+"F4.wireOp",EDGE,"E40.2.23")])]})});
            var Q35;
            Q35=makeQuery(id+"F6.boolean.opBoolean","COPY",EDGE,{"derivedFrom":makeQuery(id+"F6.opExtrude","SWEPT_EDGE",EDGE,{"disambiguationData":[OSD([sQuery(id+"F4.wireOp",EDGE,"E40.2.9"),sQuery(id+"F4.wireOp",EDGE,"E40.2.14")])]})});
            var Q36;
            Q36=makeQuery(id+"F5.boolean.opBoolean","COPY",EDGE,{"derivedFrom":makeQuery(id+"F5.opExtrude","SWEPT_EDGE",EDGE,{"disambiguationData":[OSD([sQuery(id+"F4.wireOp",EDGE,"E40.2.4"),sQuery(id+"F4.wireOp",EDGE,"E40.2.7")])]})});
            var Q37;
            Q37=makeQuery(id+"F5.boolean.opBoolean","COPY",EDGE,{"derivedFrom":makeQuery(id+"F5.opExtrude","SWEPT_EDGE",EDGE,{"disambiguationData":[OSD([sQuery(id+"F4.wireOp",EDGE,"E40.2.1"),sQuery(id+"F4.wireOp",EDGE,"E40.2.15")])]})});
            var Q38;
            Q38=makeQuery(id+"F5.boolean.opBoolean","COPY",EDGE,{"derivedFrom":makeQuery(id+"F5.opExtrude","SWEPT_EDGE",EDGE,{"disambiguationData":[OSD([sQuery(id+"F4.wireOp",EDGE,"E40.2.4"),sQuery(id+"F4.wireOp",EDGE,"E40.2.8")])]})});
            var Q39;
            Q39=makeQuery(id+"F5.boolean.opBoolean","COPY",EDGE,{"derivedFrom":makeQuery(id+"F5.opExtrude","SWEPT_EDGE",EDGE,{"disambiguationData":[OSD([sQuery(id+"F4.wireOp",EDGE,"E40.2.1"),sQuery(id+"F4.wireOp",EDGE,"E40.2.2")])]})});
            var Q40;
            Q40=makeQuery(id+"F6.boolean.opBoolean","COPY",EDGE,{"derivedFrom":makeQuery(id+"F6.opExtrude","SWEPT_EDGE",EDGE,{"disambiguationData":[OSD([sQuery(id+"F4.wireOp",EDGE,"E40.2.6"),sQuery(id+"F4.wireOp",EDGE,"E40.2.10")])]})});
            var Q41;
            Q41=makeQuery(id+"F6.boolean.opBoolean","COPY",EDGE,{"derivedFrom":makeQuery(id+"F6.opExtrude","SWEPT_EDGE",EDGE,{"disambiguationData":[OSD([sQuery(id+"F4.wireOp",EDGE,"E40.2.12"),sQuery(id+"F4.wireOp",EDGE,"E40.2.13")])]})});
            var Q42;
            Q42=makeQuery(id+"F6.boolean.opBoolean","COPY",EDGE,{"derivedFrom":makeQuery(id+"F6.opExtrude","SWEPT_EDGE",EDGE,{"disambiguationData":[OSD([sQuery(id+"F4.wireOp",EDGE,"E40.2.5"),sQuery(id+"F4.wireOp",EDGE,"E40.2.12")])]})});
            var Q43;
            Q43=makeQuery(id+"F6.boolean.opBoolean","COPY",EDGE,{"derivedFrom":makeQuery(id+"F6.opExtrude","SWEPT_EDGE",EDGE,{"disambiguationData":[OSD([sQuery(id+"F4.wireOp",EDGE,"E40.2.10"),sQuery(id+"F4.wireOp",EDGE,"E40.2.16")])]})});
            var Q44;
            Q44=makeQuery(id+"F6.boolean.opBoolean","COPY",EDGE,{"derivedFrom":makeQuery(id+"F6.opExtrude","SWEPT_EDGE",EDGE,{"disambiguationData":[OSD([sQuery(id+"F4.wireOp",EDGE,"E40.2.11"),sQuery(id+"F4.wireOp",EDGE,"E40.2.20")])]})});
            var Q45;
            Q45=makeQuery(id+"F6.boolean.opBoolean","COPY",EDGE,{"derivedFrom":makeQuery(id+"F6.opExtrude","SWEPT_EDGE",EDGE,{"disambiguationData":[OSD([sQuery(id+"F4.wireOp",EDGE,"E40.2.14"),sQuery(id+"F4.wireOp",EDGE,"E40.2.22")])]})});
            var Q46;
            Q46=makeQuery(id+"F6.boolean.opBoolean","COPY",EDGE,{"derivedFrom":makeQuery(id+"F6.opExtrude","SWEPT_EDGE",EDGE,{"disambiguationData":[OSD([sQuery(id+"F4.wireOp",EDGE,"E40.2.17"),sQuery(id+"F4.wireOp",EDGE,"E40.2.22")])]})});
            var Q47;
            Q47=makeQuery(id+"F6.boolean.opBoolean","COPY",EDGE,{"derivedFrom":makeQuery(id+"F6.opExtrude","SWEPT_EDGE",EDGE,{"disambiguationData":[OSD([sQuery(id+"F4.wireOp",EDGE,"E40.2.3"),sQuery(id+"F4.wireOp",EDGE,"E40.2.20")])]})});
            var Q48;
            Q48=makeQuery(id+"F5.boolean.opBoolean","COPY",EDGE,{"derivedFrom":makeQuery(id+"F5.opExtrude","SWEPT_EDGE",EDGE,{"disambiguationData":[OSD([sQuery(id+"F4.wireOp",EDGE,"E40.1.4"),sQuery(id+"F4.wireOp",EDGE,"E40.1.7")])]})});
            var Q49;
            Q49=makeQuery(id+"F5.boolean.opBoolean","COPY",EDGE,{"derivedFrom":makeQuery(id+"F5.opExtrude","SWEPT_EDGE",EDGE,{"disambiguationData":[OSD([sQuery(id+"F4.wireOp",EDGE,"E40.1.1"),sQuery(id+"F4.wireOp",EDGE,"E40.1.15")])]})});
            var Q50;
            Q50=makeQuery(id+"F6.boolean.opBoolean","COPY",EDGE,{"derivedFrom":makeQuery(id+"F6.opExtrude","SWEPT_EDGE",EDGE,{"disambiguationData":[OSD([sQuery(id+"F4.wireOp",EDGE,"E40.1.10"),sQuery(id+"F4.wireOp",EDGE,"E40.1.16")])]})});
            var Q51;
            Q51=makeQuery(id+"F6.boolean.opBoolean","COPY",EDGE,{"derivedFrom":makeQuery(id+"F6.opExtrude","SWEPT_EDGE",EDGE,{"disambiguationData":[OSD([sQuery(id+"F4.wireOp",EDGE,"E40.1.5"),sQuery(id+"F4.wireOp",EDGE,"E40.1.12")])]})});
            var Q52;
            Q52=makeQuery(id+"F6.boolean.opBoolean","COPY",EDGE,{"derivedFrom":makeQuery(id+"F6.opExtrude","SWEPT_EDGE",EDGE,{"disambiguationData":[OSD([sQuery(id+"F4.wireOp",EDGE,"E40.1.3"),sQuery(id+"F4.wireOp",EDGE,"E40.1.20")])]})});
            var Q53;
            Q53=makeQuery(id+"F6.boolean.opBoolean","COPY",EDGE,{"derivedFrom":makeQuery(id+"F6.opExtrude","SWEPT_EDGE",EDGE,{"disambiguationData":[OSD([sQuery(id+"F4.wireOp",EDGE,"E40.1.17"),sQuery(id+"F4.wireOp",EDGE,"E40.1.22")])]})});
            var Q54;
            Q54=makeQuery(id+"F5.boolean.opBoolean","COPY",EDGE,{"derivedFrom":makeQuery(id+"F5.opExtrude","SWEPT_EDGE",EDGE,{"disambiguationData":[OSD([sQuery(id+"F4.wireOp",EDGE,"E40.1.4"),sQuery(id+"F4.wireOp",EDGE,"E40.1.8")])]})});
            var Q55;
            Q55=makeQuery(id+"F5.boolean.opBoolean","COPY",EDGE,{"derivedFrom":makeQuery(id+"F5.opExtrude","SWEPT_EDGE",EDGE,{"disambiguationData":[OSD([sQuery(id+"F4.wireOp",EDGE,"E40.1.1"),sQuery(id+"F4.wireOp",EDGE,"E40.1.2")])]})});
            var Q56;
            Q56=makeQuery(id+"F6.boolean.opBoolean","COPY",EDGE,{"derivedFrom":makeQuery(id+"F6.opExtrude","SWEPT_EDGE",EDGE,{"disambiguationData":[OSD([sQuery(id+"F4.wireOp",EDGE,"E40.1.6"),sQuery(id+"F4.wireOp",EDGE,"E40.1.10")])]})});
            var Q57;
            Q57=makeQuery(id+"F6.boolean.opBoolean","COPY",EDGE,{"derivedFrom":makeQuery(id+"F6.opExtrude","SWEPT_EDGE",EDGE,{"disambiguationData":[OSD([sQuery(id+"F4.wireOp",EDGE,"E40.1.12"),sQuery(id+"F4.wireOp",EDGE,"E40.1.13")])]})});
            var Q58;
            Q58=makeQuery(id+"F6.boolean.opBoolean","COPY",EDGE,{"derivedFrom":makeQuery(id+"F6.opExtrude","SWEPT_EDGE",EDGE,{"disambiguationData":[OSD([sQuery(id+"F4.wireOp",EDGE,"E40.1.11"),sQuery(id+"F4.wireOp",EDGE,"E40.1.20")])]})});
            var Q59;
            Q59=makeQuery(id+"F6.boolean.opBoolean","COPY",EDGE,{"derivedFrom":makeQuery(id+"F6.opExtrude","SWEPT_EDGE",EDGE,{"disambiguationData":[OSD([sQuery(id+"F4.wireOp",EDGE,"E40.1.14"),sQuery(id+"F4.wireOp",EDGE,"E40.1.22")])]})});
            var Q60;
            Q60=makeQuery(id+"F6.boolean.opBoolean","COPY",EDGE,{"derivedFrom":makeQuery(id+"F6.opExtrude","SWEPT_EDGE",EDGE,{"disambiguationData":[OSD([sQuery(id+"F4.wireOp",EDGE,"E40.1.9"),sQuery(id+"F4.wireOp",EDGE,"E40.1.14")])]})});
            var Q61;
            Q61=makeQuery(id+"F6.boolean.opBoolean","COPY",EDGE,{"derivedFrom":makeQuery(id+"F6.opExtrude","SWEPT_EDGE",EDGE,{"disambiguationData":[OSD([sQuery(id+"F4.wireOp",EDGE,"E40.1.11"),sQuery(id+"F4.wireOp",EDGE,"E40.1.23")])]})});
            var Q62;
            Q62=makeQuery(id+"F6.boolean.opBoolean","COPY",EDGE,{"derivedFrom":makeQuery(id+"F6.opExtrude","SWEPT_EDGE",EDGE,{"disambiguationData":[OSD([sQuery(id+"F4.wireOp",EDGE,"E40.1.13"),sQuery(id+"F4.wireOp",EDGE,"E40.1.19")])]})});
            var Q63;
            Q63=makeQuery(id+"F6.boolean.opBoolean","COPY",EDGE,{"derivedFrom":makeQuery(id+"F6.opExtrude","SWEPT_EDGE",EDGE,{"disambiguationData":[OSD([sQuery(id+"F4.wireOp",EDGE,"E40.1.6"),sQuery(id+"F4.wireOp",EDGE,"E40.1.21")])]})});
            var Q64;
            Q64=makeQuery(id+"F5.boolean.opBoolean","COPY",EDGE,{"derivedFrom":makeQuery(id+"F5.opExtrude","SWEPT_EDGE",EDGE,{"disambiguationData":[OSD([sQuery(id+"F4.wireOp",EDGE,"E40.1.0"),sQuery(id+"F4.wireOp",EDGE,"E40.1.2")])]})});
            var Q65;
            Q65=makeQuery(id+"F5.boolean.opBoolean","COPY",EDGE,{"derivedFrom":makeQuery(id+"F5.opExtrude","SWEPT_EDGE",EDGE,{"disambiguationData":[OSD([sQuery(id+"F4.wireOp",EDGE,"E40.1.8"),sQuery(id+"F4.wireOp",EDGE,"E40.1.18")])]})});
            var Q66;
            Q66=makeQuery(id+"F5.boolean.opBoolean","COPY",EDGE,{"derivedFrom":makeQuery(id+"F5.opExtrude","SWEPT_EDGE",EDGE,{"disambiguationData":[OSD([sQuery(id+"F4.wireOp",EDGE,"E40.1.7"),sQuery(id+"F4.wireOp",EDGE,"E40.1.18")])]})});
            var Q67;
            Q67=makeQuery(id+"F5.boolean.opBoolean","COPY",EDGE,{"derivedFrom":makeQuery(id+"F5.opExtrude","SWEPT_EDGE",EDGE,{"disambiguationData":[OSD([sQuery(id+"F4.wireOp",EDGE,"E40.1.0"),sQuery(id+"F4.wireOp",EDGE,"E40.1.15")])]})});
            var Q68;
            Q68=makeQuery(id+"F6.boolean.opBoolean","COPY",EDGE,{"derivedFrom":makeQuery(id+"F6.opExtrude","SWEPT_EDGE",EDGE,{"disambiguationData":[OSD([sQuery(id+"F4.wireOp",EDGE,"E40.1.5"),sQuery(id+"F4.wireOp",EDGE,"E40.1.19")])]})});
            var Q69;
            Q69=makeQuery(id+"F6.boolean.opBoolean","COPY",EDGE,{"derivedFrom":makeQuery(id+"F6.opExtrude","SWEPT_EDGE",EDGE,{"disambiguationData":[OSD([sQuery(id+"F4.wireOp",EDGE,"E40.1.16"),sQuery(id+"F4.wireOp",EDGE,"E40.1.21")])]})});
            var Q70;
            Q70=makeQuery(id+"F6.boolean.opBoolean","COPY",EDGE,{"derivedFrom":makeQuery(id+"F6.opExtrude","SWEPT_EDGE",EDGE,{"disambiguationData":[OSD([sQuery(id+"F4.wireOp",EDGE,"E40.1.3"),sQuery(id+"F4.wireOp",EDGE,"E40.1.23")])]})});
            var Q71;
            Q71=makeQuery(id+"F6.boolean.opBoolean","COPY",EDGE,{"derivedFrom":makeQuery(id+"F6.opExtrude","SWEPT_EDGE",EDGE,{"disambiguationData":[OSD([sQuery(id+"F4.wireOp",EDGE,"E40.1.9"),sQuery(id+"F4.wireOp",EDGE,"E40.1.17")])]})});
            var Q72;
            Q72=makeQuery(id+"F5.boolean.opBoolean","COPY",EDGE,{"derivedFrom":makeQuery(id+"F5.opExtrude","SWEPT_EDGE",EDGE,{"disambiguationData":[OSD([sQuery(id+"F4.wireOp",EDGE,"E20"),sQuery(id+"F4.wireOp",EDGE,"E27.trimOffspring")])]})});
            var Q73;
            Q73=makeQuery(id+"F5.boolean.opBoolean","COPY",EDGE,{"derivedFrom":makeQuery(id+"F5.opExtrude","SWEPT_EDGE",EDGE,{"disambiguationData":[OSD([sQuery(id+"F4.wireOp",EDGE,"E22"),sQuery(id+"F4.wireOp",EDGE,"E26.trimOffspring")])]})});
            var Q74;
            Q74=makeQuery(id+"F6.boolean.opBoolean","COPY",EDGE,{"derivedFrom":makeQuery(id+"F6.opExtrude","SWEPT_EDGE",EDGE,{"disambiguationData":[OSD([sQuery(id+"F4.wireOp",EDGE,"E28"),sQuery(id+"F4.wireOp",EDGE,"E31.trimOffspring")])]})});
            var Q75;
            Q75=makeQuery(id+"F6.boolean.opBoolean","COPY",EDGE,{"derivedFrom":makeQuery(id+"F6.opExtrude","SWEPT_EDGE",EDGE,{"disambiguationData":[OSD([sQuery(id+"F4.wireOp",EDGE,"E32"),sQuery(id+"F4.wireOp",EDGE,"E35.trimOffspring")])]})});
            var Q76;
            Q76=makeQuery(id+"F6.boolean.opBoolean","COPY",EDGE,{"derivedFrom":makeQuery(id+"F6.opExtrude","SWEPT_EDGE",EDGE,{"disambiguationData":[OSD([sQuery(id+"F4.wireOp",EDGE,"E36"),sQuery(id+"F4.wireOp",EDGE,"E38.trimOffspring")])]})});
            var Q77;
            Q77=makeQuery(id+"F6.boolean.opBoolean","COPY",EDGE,{"derivedFrom":makeQuery(id+"F6.opExtrude","SWEPT_EDGE",EDGE,{"disambiguationData":[OSD([sQuery(id+"F4.wireOp",EDGE,"E17"),sQuery(id+"F4.wireOp",EDGE,"E19")])]})});
            var Q78;
            Q78=makeQuery(id+"F5.boolean.opBoolean","COPY",EDGE,{"derivedFrom":makeQuery(id+"F5.opExtrude","SWEPT_EDGE",EDGE,{"disambiguationData":[OSD([sQuery(id+"F4.wireOp",EDGE,"E16"),sQuery(id+"F4.wireOp",EDGE,"E27.trimOffspring")])]})});
            var Q79;
            Q79=makeQuery(id+"F5.boolean.opBoolean","COPY",EDGE,{"derivedFrom":makeQuery(id+"F5.opExtrude","SWEPT_EDGE",EDGE,{"disambiguationData":[OSD([sQuery(id+"F4.wireOp",EDGE,"E21"),sQuery(id+"F4.wireOp",EDGE,"E26.trimOffspring")])]})});
            var Q80;
            Q80=makeQuery(id+"F6.boolean.opBoolean","COPY",EDGE,{"derivedFrom":makeQuery(id+"F6.opExtrude","SWEPT_EDGE",EDGE,{"disambiguationData":[OSD([sQuery(id+"F4.wireOp",EDGE,"E23"),sQuery(id+"F4.wireOp",EDGE,"E31.trimOffspring")])]})});
            var Q81;
            Q81=makeQuery(id+"F6.boolean.opBoolean","COPY",EDGE,{"derivedFrom":makeQuery(id+"F6.opExtrude","SWEPT_EDGE",EDGE,{"disambiguationData":[OSD([sQuery(id+"F4.wireOp",EDGE,"E29"),sQuery(id+"F4.wireOp",EDGE,"E35.trimOffspring")])]})});
            var Q82;
            Q82=makeQuery(id+"F6.boolean.opBoolean","COPY",EDGE,{"derivedFrom":makeQuery(id+"F6.opExtrude","SWEPT_EDGE",EDGE,{"disambiguationData":[OSD([sQuery(id+"F4.wireOp",EDGE,"E33"),sQuery(id+"F4.wireOp",EDGE,"E38.trimOffspring")])]})});
            var Q83;
            Q83=makeQuery(id+"F6.boolean.opBoolean","COPY",EDGE,{"derivedFrom":makeQuery(id+"F6.opExtrude","SWEPT_EDGE",EDGE,{"disambiguationData":[OSD([sQuery(id+"F4.wireOp",EDGE,"E19"),sQuery(id+"F4.wireOp",EDGE,"E37")])]})});
            var Q84;
            Q84=makeQuery(id+"F6.boolean.opBoolean","COPY",EDGE,{"derivedFrom":makeQuery(id+"F6.opExtrude","SWEPT_EDGE",EDGE,{"disambiguationData":[OSD([sQuery(id+"F4.wireOp",EDGE,"E17"),sQuery(id+"F4.wireOp",EDGE,"E18")])]})});
            var Q85;
            Q85=makeQuery(id+"F6.boolean.opBoolean","COPY",EDGE,{"derivedFrom":makeQuery(id+"F6.opExtrude","SWEPT_EDGE",EDGE,{"disambiguationData":[OSD([sQuery(id+"F4.wireOp",EDGE,"E36"),sQuery(id+"F4.wireOp",EDGE,"E39.trimOffspring")])]})});
            var Q86;
            Q86=makeQuery(id+"F6.boolean.opBoolean","COPY",EDGE,{"derivedFrom":makeQuery(id+"F6.opExtrude","SWEPT_EDGE",EDGE,{"disambiguationData":[OSD([sQuery(id+"F4.wireOp",EDGE,"E32"),sQuery(id+"F4.wireOp",EDGE,"E34.trimOffspring")])]})});
            var Q87;
            Q87=makeQuery(id+"F6.boolean.opBoolean","COPY",EDGE,{"derivedFrom":makeQuery(id+"F6.opExtrude","SWEPT_EDGE",EDGE,{"disambiguationData":[OSD([sQuery(id+"F4.wireOp",EDGE,"E28"),sQuery(id+"F4.wireOp",EDGE,"E30.trimOffspring")])]})});
            var Q88;
            Q88=makeQuery(id+"F5.boolean.opBoolean","COPY",EDGE,{"derivedFrom":makeQuery(id+"F5.opExtrude","SWEPT_EDGE",EDGE,{"disambiguationData":[OSD([sQuery(id+"F4.wireOp",EDGE,"E20"),sQuery(id+"F4.wireOp",EDGE,"E25.trimOffspring")])]})});
            var Q89;
            Q89=makeQuery(id+"F5.boolean.opBoolean","COPY",EDGE,{"derivedFrom":makeQuery(id+"F5.opExtrude","SWEPT_EDGE",EDGE,{"disambiguationData":[OSD([sQuery(id+"F4.wireOp",EDGE,"E22"),sQuery(id+"F4.wireOp",EDGE,"E24.trimOffspring")])]})});
            var Q90;
            Q90=makeQuery(id+"F5.boolean.opBoolean","COPY",EDGE,{"derivedFrom":makeQuery(id+"F5.opExtrude","SWEPT_EDGE",EDGE,{"disambiguationData":[OSD([sQuery(id+"F4.wireOp",EDGE,"E16"),sQuery(id+"F4.wireOp",EDGE,"E25.trimOffspring")])]})});
            var Q91;
            Q91=makeQuery(id+"F5.boolean.opBoolean","COPY",EDGE,{"derivedFrom":makeQuery(id+"F5.opExtrude","SWEPT_EDGE",EDGE,{"disambiguationData":[OSD([sQuery(id+"F4.wireOp",EDGE,"E21"),sQuery(id+"F4.wireOp",EDGE,"E24.trimOffspring")])]})});
            var Q92;
            Q92=makeQuery(id+"F6.boolean.opBoolean","COPY",EDGE,{"derivedFrom":makeQuery(id+"F6.opExtrude","SWEPT_EDGE",EDGE,{"disambiguationData":[OSD([sQuery(id+"F4.wireOp",EDGE,"E23"),sQuery(id+"F4.wireOp",EDGE,"E30.trimOffspring")])]})});
            var Q93;
            Q93=makeQuery(id+"F6.boolean.opBoolean","COPY",EDGE,{"derivedFrom":makeQuery(id+"F6.opExtrude","SWEPT_EDGE",EDGE,{"disambiguationData":[OSD([sQuery(id+"F4.wireOp",EDGE,"E29"),sQuery(id+"F4.wireOp",EDGE,"E34.trimOffspring")])]})});
            var Q94;
            Q94=makeQuery(id+"F6.boolean.opBoolean","COPY",EDGE,{"derivedFrom":makeQuery(id+"F6.opExtrude","SWEPT_EDGE",EDGE,{"disambiguationData":[OSD([sQuery(id+"F4.wireOp",EDGE,"E33"),sQuery(id+"F4.wireOp",EDGE,"E39.trimOffspring")])]})});
            var Q95;
            Q95=makeQuery(id+"F6.boolean.opBoolean","COPY",EDGE,{"derivedFrom":makeQuery(id+"F6.opExtrude","SWEPT_EDGE",EDGE,{"disambiguationData":[OSD([sQuery(id+"F4.wireOp",EDGE,"E18"),sQuery(id+"F4.wireOp",EDGE,"E37")])]})});
            fillet(context, id + "F7", {"entities" : qUnion([Q0, Q1, Q2, Q3, Q4, Q5, Q6, Q7, Q8, Q9, Q10, Q11, Q12, Q13, Q14, Q15, Q16, Q17, Q18, Q19, Q20, Q21, Q22, Q23, Q24, Q25, Q26, Q27, Q28, Q29, Q30, Q31, Q32, Q33, Q34, Q35, Q36, Q37, Q38, Q39, Q40, Q41, Q42, Q43, Q44, Q45, Q46, Q47, Q48, Q49, Q50, Q51, Q52, Q53, Q54, Q55, Q56, Q57, Q58, Q59, Q60, Q61, Q62, Q63, Q64, Q65, Q66, Q67, Q68, Q69, Q70, Q71, Q72, Q73, Q74, Q75, Q76, Q77, Q78, Q79, Q80, Q81, Q82, Q83, Q84, Q85, Q86, Q87, Q88, Q89, Q90, Q91, Q92, Q93, Q94, Q95]), "radius" : 2 * mm, "tangentPropagation" : true, "allowEdgeOverflow" : false});
        }
    });
